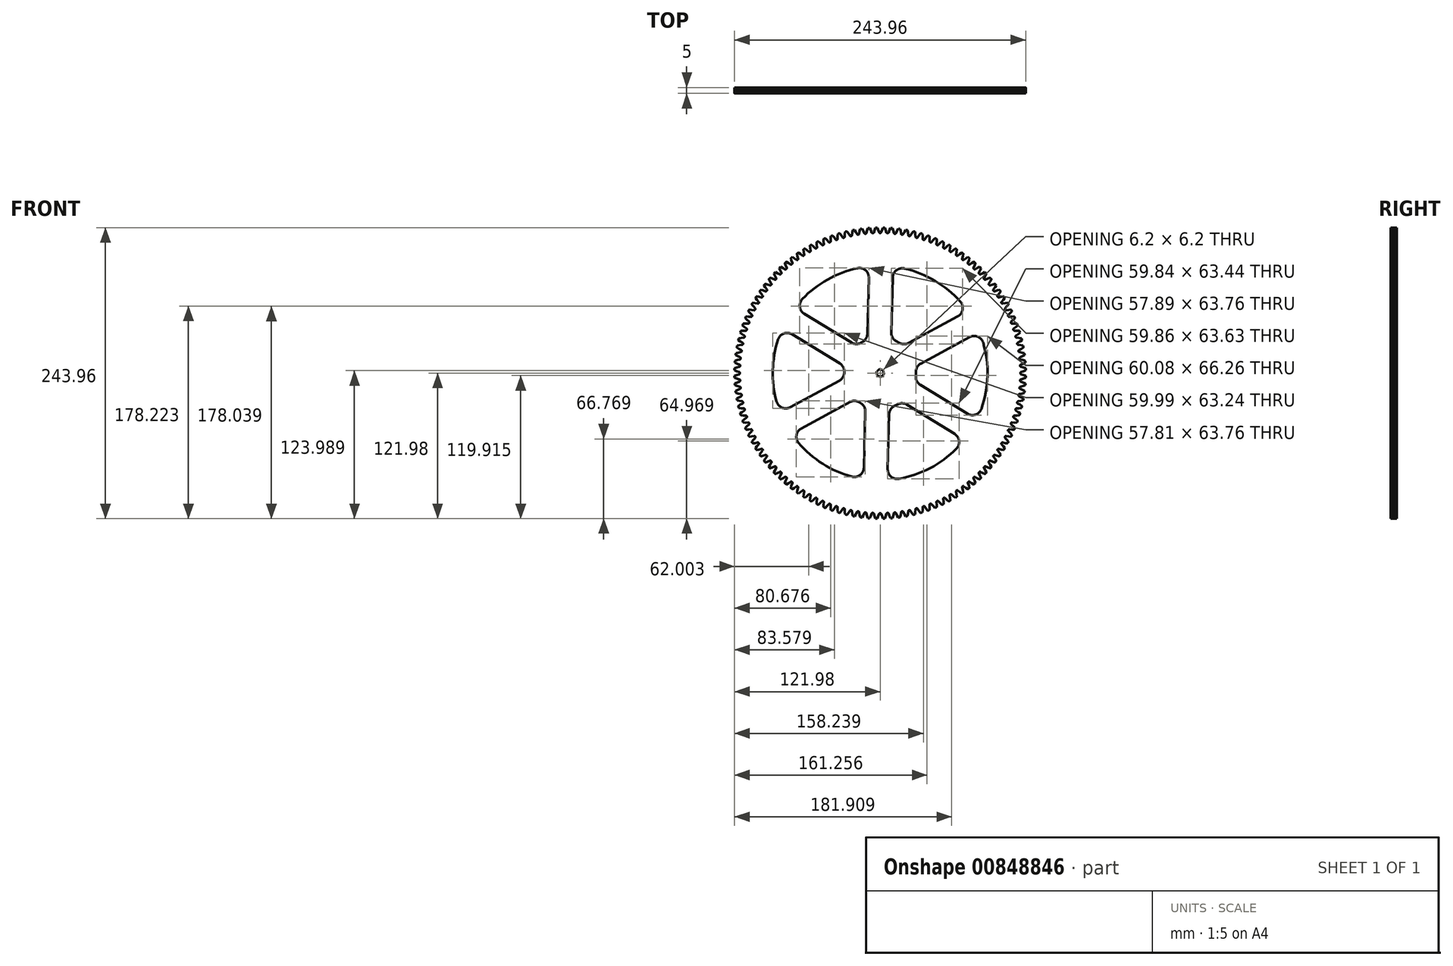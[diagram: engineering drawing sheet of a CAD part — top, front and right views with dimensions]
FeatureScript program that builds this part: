
annotation { "Feature Type Name" : "Feature", "Feature Type Description" : "" }
export const myFeature = defineFeature(function(context is Context, id is Id, definition is map)
    precondition{}
    {
        {
            var Q0;
            Q0=qCreatedBy(makeId("Front.planeOp"),FACE);
            var sketch = newSketch(context, id + "F0", { "sketchPlane" : qUnion([Q0])});
            skArc(sketch, "E0", {"start": v(-16.1, -25.31) * mm, "mid": v(-16.55, -25.02) * mm, "end": v(-16.99, -24.73) * mm});
            skArc(sketch, "E1", {"start": v(-16.1, -25.31) * mm, "mid": v(-13.33, -28.3) * mm, "end": v(-12.4, -32.27) * mm});
            skLineSegment(sketch, "E2", {"start": v(-12.4, -32.27) * mm, "end": v(-13.63, -79.3) * mm});
            skArc(sketch, "E3", {"start": v(-13.63, -79.3) * mm, "mid": v(-16.86, -85.52) * mm, "end": v(-23.74, -86.81) * mm});
            skArc(sketch, "E4", {"start": v(-23.74, -86.81) * mm, "mid": v(-48.12, -76.05) * mm, "end": v(-68.28, -58.63) * mm});
            skArc(sketch, "E5", {"start": v(-68.28, -58.63) * mm, "mid": v(-70.08, -51.97) * mm, "end": v(-66.03, -46.39) * mm});
            skLineSegment(sketch, "E6", {"start": v(-25.33, -24.3) * mm, "end": v(-66.03, -46.39) * mm});
            skArc(sketch, "E7", {"start": v(-25.33, -24.3) * mm, "mid": v(-21.1, -23.33) * mm, "end": v(-16.99, -24.73) * mm});
            skArc(sketch, "E8", {"start": v(-30, 0.55) * mm, "mid": v(-30, 0.75) * mm, "end": v(-29.98, 0.96) * mm});
            skArc(sketch, "E9", {"start": v(-30, 0.55) * mm, "mid": v(-31.16, -3.46) * mm, "end": v(-34.18, -6.33) * mm});
            skLineSegment(sketch, "E10", {"start": v(-34.18, -6.33) * mm, "end": v(-75.28, -28.65) * mm});
            skArc(sketch, "E11", {"start": v(-75.28, -28.65) * mm, "mid": v(-82.24, -28.98) * mm, "end": v(-86.82, -23.73) * mm});
            skArc(sketch, "E12", {"start": v(-86.82, -23.73) * mm, "mid": v(-89.97, 2.32) * mm, "end": v(-85.48, 28.17) * mm});
            skArc(sketch, "E13", {"start": v(-85.48, 28.17) * mm, "mid": v(-80.63, 33.18) * mm, "end": v(-73.7, 32.49) * mm});
            skLineSegment(sketch, "E14", {"start": v(-33.8, 8.04) * mm, "end": v(-73.7, 32.49) * mm});
            skArc(sketch, "E15", {"start": v(-33.8, 8.04) * mm, "mid": v(-30.94, 5.01) * mm, "end": v(-29.98, 0.96) * mm});
            skLineSegment(sketch, "E16", {"start": v(34.17, 8.01) * mm, "end": v(74.87, 30.1) * mm});
            skArc(sketch, "E17", {"start": v(74.87, 30.1) * mm, "mid": v(81.76, 30.46) * mm, "end": v(86.36, 25.33) * mm});
            skArc(sketch, "E18", {"start": v(86.36, 25.33) * mm, "mid": v(89.97, -2.4) * mm, "end": v(84.89, -29.9) * mm});
            skArc(sketch, "E19", {"start": v(84.89, -29.9) * mm, "mid": v(80.02, -34.78) * mm, "end": v(73.16, -34.06) * mm});
            skLineSegment(sketch, "E20", {"start": v(33.7, -9.87) * mm, "end": v(73.16, -34.06) * mm});
            skArc(sketch, "E21", {"start": v(33.7, -9.87) * mm, "mid": v(30.75, -6.68) * mm, "end": v(29.9, -2.4) * mm});
            skArc(sketch, "E22", {"start": v(29.99, 0.78) * mm, "mid": v(29.99, -0.82) * mm, "end": v(29.9, -2.4) * mm});
            skArc(sketch, "E23", {"start": v(29.99, 0.78) * mm, "mid": v(31.06, 4.98) * mm, "end": v(34.17, 8.01) * mm});
            skArc(sketch, "E24", {"start": v(13.7, 26.7) * mm, "mid": v(14.8, 26.1) * mm, "end": v(15.88, 25.45) * mm});
            skArc(sketch, "E25", {"start": v(13.7, 26.7) * mm, "mid": v(10.46, 29.73) * mm, "end": v(9.35, 34.02) * mm});
            skLineSegment(sketch, "E26", {"start": v(9.35, 34.02) * mm, "end": v(10.55, 80.08) * mm});
            skArc(sketch, "E27", {"start": v(10.55, 80.08) * mm, "mid": v(13.66, 86.2) * mm, "end": v(20.36, 87.67) * mm});
            skArc(sketch, "E28", {"start": v(20.36, 87.67) * mm, "mid": v(45.93, 77.4) * mm, "end": v(67.19, 59.88) * mm});
            skArc(sketch, "E29", {"start": v(67.19, 59.88) * mm, "mid": v(69.1, 53.18) * mm, "end": v(65.03, 47.53) * mm});
            skLineSegment(sketch, "E30", {"start": v(23.93, 25.21) * mm, "end": v(65.03, 47.53) * mm});
            skArc(sketch, "E31", {"start": v(23.93, 25.21) * mm, "mid": v(19.87, 24.25) * mm, "end": v(15.88, 25.45) * mm});
            skArc(sketch, "E32", {"start": v(12.05, 116.88) * mm, "mid": v(12.28, 116.86) * mm, "end": v(12.52, 116.83) * mm});
            skArc(sketch, "E33", {"start": v(12.05, 116.88) * mm, "mid": v(11.67, 117.05) * mm, "end": v(11.47, 117.4) * mm});
            skLineSegment(sketch, "E34", {"start": v(10.94, 119.67) * mm, "end": v(10.38, 121.56) * mm});
            skLineSegment(sketch, "E35", {"start": v(11.47, 117.4) * mm, "end": v(10.94, 119.67) * mm});
            skArc(sketch, "E36", {"start": v(8.76, 121.68) * mm, "mid": v(9.57, 121.62) * mm, "end": v(10.38, 121.56) * mm});
            skLineSegment(sketch, "E37", {"start": v(7.92, 119.9) * mm, "end": v(8.76, 121.68) * mm});
            skLineSegment(sketch, "E38", {"start": v(7.04, 117.75) * mm, "end": v(7.92, 119.9) * mm});
            skArc(sketch, "E39", {"start": v(7.04, 117.75) * mm, "mid": v(6.78, 117.43) * mm, "end": v(6.39, 117.33) * mm});
            skArc(sketch, "E40", {"start": v(5.91, 117.35) * mm, "mid": v(6.15, 117.34) * mm, "end": v(6.39, 117.33) * mm});
            skArc(sketch, "E41", {"start": v(5.91, 117.35) * mm, "mid": v(5.53, 117.5) * mm, "end": v(5.3, 117.84) * mm});
            skLineSegment(sketch, "E42", {"start": v(4.66, 120.08) * mm, "end": v(4, 121.93) * mm});
            skLineSegment(sketch, "E43", {"start": v(5.3, 117.84) * mm, "end": v(4.66, 120.08) * mm});
            skArc(sketch, "E44", {"start": v(2.38, 121.98) * mm, "mid": v(3.2, 121.96) * mm, "end": v(4, 121.93) * mm});
            skLineSegment(sketch, "E45", {"start": v(1.63, 120.15) * mm, "end": v(2.38, 121.98) * mm});
            skLineSegment(sketch, "E46", {"start": v(0.86, 117.96) * mm, "end": v(1.63, 120.15) * mm});
            skArc(sketch, "E47", {"start": v(0.86, 117.96) * mm, "mid": v(0.63, 117.63) * mm, "end": v(0.24, 117.5) * mm});
            skArc(sketch, "E48", {"start": v(-0.24, 117.5) * mm, "mid": v(0, 117.5) * mm, "end": v(0.24, 117.5) * mm});
            skArc(sketch, "E49", {"start": v(-0.24, 117.5) * mm, "mid": v(-0.63, 117.63) * mm, "end": v(-0.86, 117.96) * mm});
            skLineSegment(sketch, "E50", {"start": v(-1.63, 120.15) * mm, "end": v(-2.38, 121.98) * mm});
            skLineSegment(sketch, "E51", {"start": v(-0.86, 117.96) * mm, "end": v(-1.63, 120.15) * mm});
            skArc(sketch, "E52", {"start": v(-4, 121.93) * mm, "mid": v(-3.2, 121.96) * mm, "end": v(-2.38, 121.98) * mm});
            skLineSegment(sketch, "E53", {"start": v(-4.66, 120.08) * mm, "end": v(-4, 121.93) * mm});
            skLineSegment(sketch, "E54", {"start": v(-5.3, 117.84) * mm, "end": v(-4.66, 120.08) * mm});
            skArc(sketch, "E55", {"start": v(-5.3, 117.84) * mm, "mid": v(-5.53, 117.5) * mm, "end": v(-5.91, 117.35) * mm});
            skArc(sketch, "E56", {"start": v(-6.39, 117.33) * mm, "mid": v(-6.15, 117.34) * mm, "end": v(-5.91, 117.35) * mm});
            skArc(sketch, "E57", {"start": v(-6.39, 117.33) * mm, "mid": v(-6.78, 117.43) * mm, "end": v(-7.04, 117.75) * mm});
            skLineSegment(sketch, "E58", {"start": v(-7.92, 119.9) * mm, "end": v(-8.76, 121.68) * mm});
            skLineSegment(sketch, "E59", {"start": v(-7.04, 117.75) * mm, "end": v(-7.92, 119.9) * mm});
            skArc(sketch, "E60", {"start": v(-10.38, 121.56) * mm, "mid": v(-9.57, 121.62) * mm, "end": v(-8.76, 121.68) * mm});
            skLineSegment(sketch, "E61", {"start": v(-10.94, 119.67) * mm, "end": v(-10.38, 121.56) * mm});
            skLineSegment(sketch, "E62", {"start": v(-11.47, 117.4) * mm, "end": v(-10.94, 119.67) * mm});
            skArc(sketch, "E63", {"start": v(-11.47, 117.4) * mm, "mid": v(-11.67, 117.05) * mm, "end": v(-12.05, 116.88) * mm});
            skArc(sketch, "E64", {"start": v(-12.52, 116.83) * mm, "mid": v(-12.28, 116.86) * mm, "end": v(-12.05, 116.88) * mm});
            skArc(sketch, "E65", {"start": v(-12.52, 116.83) * mm, "mid": v(-12.92, 116.92) * mm, "end": v(-13.19, 117.22) * mm});
            skLineSegment(sketch, "E66", {"start": v(-14.18, 119.33) * mm, "end": v(-15.12, 121.06) * mm});
            skLineSegment(sketch, "E67", {"start": v(-13.19, 117.22) * mm, "end": v(-14.18, 119.33) * mm});
            skArc(sketch, "E68", {"start": v(-16.73, 120.85) * mm, "mid": v(-15.92, 120.96) * mm, "end": v(-15.12, 121.06) * mm});
            skLineSegment(sketch, "E69", {"start": v(-17.18, 118.93) * mm, "end": v(-16.73, 120.85) * mm});
            skLineSegment(sketch, "E70", {"start": v(-17.6, 116.64) * mm, "end": v(-17.18, 118.93) * mm});
            skArc(sketch, "E71", {"start": v(-17.6, 116.64) * mm, "mid": v(-17.78, 116.28) * mm, "end": v(-18.15, 116.1) * mm});
            skArc(sketch, "E72", {"start": v(-18.62, 116.02) * mm, "mid": v(-18.38, 116.05) * mm, "end": v(-18.15, 116.1) * mm});
            skArc(sketch, "E73", {"start": v(-18.62, 116.02) * mm, "mid": v(-19.02, 116.08) * mm, "end": v(-19.3, 116.37) * mm});
            skLineSegment(sketch, "E74", {"start": v(-20.4, 118.42) * mm, "end": v(-21.44, 120.1) * mm});
            skLineSegment(sketch, "E75", {"start": v(-19.3, 116.37) * mm, "end": v(-20.4, 118.42) * mm});
            skArc(sketch, "E76", {"start": v(-23.03, 119.8) * mm, "mid": v(-22.23, 119.96) * mm, "end": v(-21.44, 120.1) * mm});
            skLineSegment(sketch, "E77", {"start": v(-23.38, 117.87) * mm, "end": v(-23.03, 119.8) * mm});
            skLineSegment(sketch, "E78", {"start": v(-23.68, 115.56) * mm, "end": v(-23.38, 117.87) * mm});
            skArc(sketch, "E79", {"start": v(-23.68, 115.56) * mm, "mid": v(-23.84, 115.19) * mm, "end": v(-24.2, 114.98) * mm});
            skArc(sketch, "E80", {"start": v(-24.66, 114.88) * mm, "mid": v(-24.43, 114.93) * mm, "end": v(-24.2, 114.98) * mm});
            skArc(sketch, "E81", {"start": v(-24.66, 114.88) * mm, "mid": v(-25.07, 114.93) * mm, "end": v(-25.37, 115.2) * mm});
            skLineSegment(sketch, "E82", {"start": v(-26.58, 117.19) * mm, "end": v(-27.7, 118.82) * mm});
            skLineSegment(sketch, "E83", {"start": v(-25.37, 115.2) * mm, "end": v(-26.58, 117.19) * mm});
            skArc(sketch, "E84", {"start": v(-29.27, 118.44) * mm, "mid": v(-28.48, 118.63) * mm, "end": v(-27.7, 118.82) * mm});
            skLineSegment(sketch, "E85", {"start": v(-29.52, 116.48) * mm, "end": v(-29.27, 118.44) * mm});
            skLineSegment(sketch, "E86", {"start": v(-29.7, 114.16) * mm, "end": v(-29.52, 116.48) * mm});
            skArc(sketch, "E87", {"start": v(-29.7, 114.16) * mm, "mid": v(-29.84, 113.78) * mm, "end": v(-30.18, 113.56) * mm});
            skArc(sketch, "E88", {"start": v(-30.64, 113.43) * mm, "mid": v(-30.41, 113.5) * mm, "end": v(-30.18, 113.56) * mm});
            skArc(sketch, "E89", {"start": v(-30.64, 113.43) * mm, "mid": v(-31.05, 113.46) * mm, "end": v(-31.36, 113.71) * mm});
            skLineSegment(sketch, "E90", {"start": v(-32.68, 115.64) * mm, "end": v(-33.87, 117.2) * mm});
            skLineSegment(sketch, "E91", {"start": v(-31.36, 113.71) * mm, "end": v(-32.68, 115.64) * mm});
            skArc(sketch, "E92", {"start": v(-35.43, 116.74) * mm, "mid": v(-34.65, 116.98) * mm, "end": v(-33.87, 117.2) * mm});
            skLineSegment(sketch, "E93", {"start": v(-35.58, 114.78) * mm, "end": v(-35.43, 116.74) * mm});
            skLineSegment(sketch, "E94", {"start": v(-35.63, 112.45) * mm, "end": v(-35.58, 114.78) * mm});
            skArc(sketch, "E95", {"start": v(-35.63, 112.45) * mm, "mid": v(-35.75, 112.06) * mm, "end": v(-36.08, 111.82) * mm});
            skArc(sketch, "E96", {"start": v(-36.54, 111.68) * mm, "mid": v(-36.3, 111.75) * mm, "end": v(-36.08, 111.82) * mm});
            skArc(sketch, "E97", {"start": v(-36.54, 111.68) * mm, "mid": v(-36.94, 111.68) * mm, "end": v(-37.27, 111.92) * mm});
            skLineSegment(sketch, "E98", {"start": v(-38.68, 113.77) * mm, "end": v(-39.96, 115.27) * mm});
            skLineSegment(sketch, "E99", {"start": v(-37.27, 111.92) * mm, "end": v(-38.68, 113.77) * mm});
            skArc(sketch, "E100", {"start": v(-41.49, 114.73) * mm, "mid": v(-40.72, 115) * mm, "end": v(-39.96, 115.27) * mm});
            skLineSegment(sketch, "E101", {"start": v(-41.54, 112.76) * mm, "end": v(-41.49, 114.73) * mm});
            skLineSegment(sketch, "E102", {"start": v(-41.47, 110.43) * mm, "end": v(-41.54, 112.76) * mm});
            skArc(sketch, "E103", {"start": v(-41.47, 110.43) * mm, "mid": v(-41.57, 110.04) * mm, "end": v(-41.89, 109.78) * mm});
            skArc(sketch, "E104", {"start": v(-42.33, 109.61) * mm, "mid": v(-42.1, 109.7) * mm, "end": v(-41.89, 109.78) * mm});
            skArc(sketch, "E105", {"start": v(-42.33, 109.61) * mm, "mid": v(-42.74, 109.59) * mm, "end": v(-43.08, 109.81) * mm});
            skLineSegment(sketch, "E106", {"start": v(-44.58, 111.59) * mm, "end": v(-45.94, 113.02) * mm});
            skLineSegment(sketch, "E107", {"start": v(-43.08, 109.81) * mm, "end": v(-44.58, 111.59) * mm});
            skArc(sketch, "E108", {"start": v(-47.43, 112.4) * mm, "mid": v(-46.69, 112.71) * mm, "end": v(-45.94, 113.02) * mm});
            skLineSegment(sketch, "E109", {"start": v(-47.38, 110.43) * mm, "end": v(-47.43, 112.4) * mm});
            skLineSegment(sketch, "E110", {"start": v(-47.19, 108.11) * mm, "end": v(-47.38, 110.43) * mm});
            skArc(sketch, "E111", {"start": v(-47.19, 108.11) * mm, "mid": v(-47.27, 107.71) * mm, "end": v(-47.57, 107.44) * mm});
            skArc(sketch, "E112", {"start": v(-48, 107.24) * mm, "mid": v(-47.8, 107.34) * mm, "end": v(-47.57, 107.44) * mm});
            skArc(sketch, "E113", {"start": v(-48, 107.24) * mm, "mid": v(-48.42, 107.2) * mm, "end": v(-48.77, 107.4) * mm});
            skLineSegment(sketch, "E114", {"start": v(-50.36, 109.1) * mm, "end": v(-51.8, 110.46) * mm});
            skLineSegment(sketch, "E115", {"start": v(-48.77, 107.4) * mm, "end": v(-50.36, 109.1) * mm});
            skArc(sketch, "E116", {"start": v(-53.25, 109.76) * mm, "mid": v(-52.52, 110.12) * mm, "end": v(-51.8, 110.46) * mm});
            skLineSegment(sketch, "E117", {"start": v(-53.1, 107.8) * mm, "end": v(-53.25, 109.76) * mm});
            skLineSegment(sketch, "E118", {"start": v(-52.78, 105.5) * mm, "end": v(-53.1, 107.8) * mm});
            skArc(sketch, "E119", {"start": v(-52.78, 105.5) * mm, "mid": v(-52.84, 105.1) * mm, "end": v(-53.13, 104.8) * mm});
            skArc(sketch, "E120", {"start": v(-53.56, 104.58) * mm, "mid": v(-53.34, 104.7) * mm, "end": v(-53.13, 104.8) * mm});
            skArc(sketch, "E121", {"start": v(-53.56, 104.58) * mm, "mid": v(-53.96, 104.52) * mm, "end": v(-54.32, 104.7) * mm});
            skLineSegment(sketch, "E122", {"start": v(-56, 106.32) * mm, "end": v(-57.5, 107.6) * mm});
            skLineSegment(sketch, "E123", {"start": v(-54.32, 104.7) * mm, "end": v(-56, 106.32) * mm});
            skArc(sketch, "E124", {"start": v(-58.92, 106.83) * mm, "mid": v(-58.21, 107.22) * mm, "end": v(-57.5, 107.6) * mm});
            skLineSegment(sketch, "E125", {"start": v(-58.66, 104.87) * mm, "end": v(-58.92, 106.83) * mm});
            skLineSegment(sketch, "E126", {"start": v(-58.23, 102.59) * mm, "end": v(-58.66, 104.87) * mm});
            skArc(sketch, "E127", {"start": v(-58.23, 102.59) * mm, "mid": v(-58.27, 102.18) * mm, "end": v(-58.54, 101.88) * mm});
            skArc(sketch, "E128", {"start": v(-58.96, 101.64) * mm, "mid": v(-58.75, 101.76) * mm, "end": v(-58.54, 101.88) * mm});
            skArc(sketch, "E129", {"start": v(-58.96, 101.64) * mm, "mid": v(-59.36, 101.55) * mm, "end": v(-59.73, 101.72) * mm});
            skLineSegment(sketch, "E130", {"start": v(-61.5, 103.24) * mm, "end": v(-63.05, 104.44) * mm});
            skLineSegment(sketch, "E131", {"start": v(-59.73, 101.72) * mm, "end": v(-61.5, 103.24) * mm});
            skArc(sketch, "E132", {"start": v(-64.43, 103.6) * mm, "mid": v(-63.74, 104.02) * mm, "end": v(-63.05, 104.44) * mm});
            skLineSegment(sketch, "E133", {"start": v(-64.07, 101.66) * mm, "end": v(-64.43, 103.6) * mm});
            skLineSegment(sketch, "E134", {"start": v(-63.52, 99.4) * mm, "end": v(-64.07, 101.66) * mm});
            skArc(sketch, "E135", {"start": v(-63.52, 99.4) * mm, "mid": v(-63.54, 99) * mm, "end": v(-63.8, 98.67) * mm});
            skArc(sketch, "E136", {"start": v(-64.2, 98.41) * mm, "mid": v(-64, 98.54) * mm, "end": v(-63.8, 98.67) * mm});
            skArc(sketch, "E137", {"start": v(-64.2, 98.41) * mm, "mid": v(-64.59, 98.3) * mm, "end": v(-64.97, 98.46) * mm});
            skLineSegment(sketch, "E138", {"start": v(-66.8, 99.88) * mm, "end": v(-68.43, 101) * mm});
            skLineSegment(sketch, "E139", {"start": v(-64.97, 98.46) * mm, "end": v(-66.8, 99.88) * mm});
            skArc(sketch, "E140", {"start": v(-69.77, 100.08) * mm, "mid": v(-69.1, 100.54) * mm, "end": v(-68.43, 101) * mm});
            skLineSegment(sketch, "E141", {"start": v(-69.3, 98.17) * mm, "end": v(-69.77, 100.08) * mm});
            skLineSegment(sketch, "E142", {"start": v(-68.63, 95.94) * mm, "end": v(-69.3, 98.17) * mm});
            skArc(sketch, "E143", {"start": v(-68.63, 95.94) * mm, "mid": v(-68.63, 95.53) * mm, "end": v(-68.87, 95.2) * mm});
            skArc(sketch, "E144", {"start": v(-69.26, 94.92) * mm, "mid": v(-69.06, 95.06) * mm, "end": v(-68.87, 95.2) * mm});
            skArc(sketch, "E145", {"start": v(-69.26, 94.92) * mm, "mid": v(-69.65, 94.8) * mm, "end": v(-70.03, 94.92) * mm});
            skLineSegment(sketch, "E146", {"start": v(-71.95, 96.25) * mm, "end": v(-73.62, 97.28) * mm});
            skLineSegment(sketch, "E147", {"start": v(-70.03, 94.92) * mm, "end": v(-71.95, 96.25) * mm});
            skArc(sketch, "E148", {"start": v(-74.9, 96.3) * mm, "mid": v(-74.27, 96.79) * mm, "end": v(-73.62, 97.28) * mm});
            skLineSegment(sketch, "E149", {"start": v(-74.35, 94.4) * mm, "end": v(-74.9, 96.3) * mm});
            skLineSegment(sketch, "E150", {"start": v(-73.56, 92.21) * mm, "end": v(-74.35, 94.4) * mm});
            skArc(sketch, "E151", {"start": v(-73.56, 92.21) * mm, "mid": v(-73.54, 91.8) * mm, "end": v(-73.76, 91.46) * mm});
            skArc(sketch, "E152", {"start": v(-74.13, 91.16) * mm, "mid": v(-73.95, 91.31) * mm, "end": v(-73.76, 91.46) * mm});
            skArc(sketch, "E153", {"start": v(-74.13, 91.16) * mm, "mid": v(-74.51, 91.02) * mm, "end": v(-74.9, 91.13) * mm});
            skLineSegment(sketch, "E154", {"start": v(-76.88, 92.35) * mm, "end": v(-78.62, 93.3) * mm});
            skLineSegment(sketch, "E155", {"start": v(-74.9, 91.13) * mm, "end": v(-76.88, 92.35) * mm});
            skArc(sketch, "E156", {"start": v(-79.85, 92.24) * mm, "mid": v(-79.23, 92.77) * mm, "end": v(-78.62, 93.3) * mm});
            skLineSegment(sketch, "E157", {"start": v(-79.19, 90.38) * mm, "end": v(-79.85, 92.24) * mm});
            skLineSegment(sketch, "E158", {"start": v(-78.29, 88.24) * mm, "end": v(-79.19, 90.38) * mm});
            skArc(sketch, "E159", {"start": v(-78.29, 88.24) * mm, "mid": v(-78.24, 87.83) * mm, "end": v(-78.45, 87.48) * mm});
            skArc(sketch, "E160", {"start": v(-78.8, 87.16) * mm, "mid": v(-78.62, 87.32) * mm, "end": v(-78.45, 87.48) * mm});
            skArc(sketch, "E161", {"start": v(-78.8, 87.16) * mm, "mid": v(-79.17, 87) * mm, "end": v(-79.57, 87.08) * mm});
            skLineSegment(sketch, "E162", {"start": v(-81.61, 88.2) * mm, "end": v(-83.4, 89.05) * mm});
            skLineSegment(sketch, "E163", {"start": v(-79.57, 87.08) * mm, "end": v(-81.61, 88.2) * mm});
            skArc(sketch, "E164", {"start": v(-84.56, 87.94) * mm, "mid": v(-83.98, 88.5) * mm, "end": v(-83.4, 89.05) * mm});
            skLineSegment(sketch, "E165", {"start": v(-83.8, 86.12) * mm, "end": v(-84.56, 87.94) * mm});
            skLineSegment(sketch, "E166", {"start": v(-82.8, 84.02) * mm, "end": v(-83.8, 86.12) * mm});
            skArc(sketch, "E167", {"start": v(-82.8, 84.02) * mm, "mid": v(-82.73, 83.62) * mm, "end": v(-82.92, 83.25) * mm});
            skArc(sketch, "E168", {"start": v(-83.25, 82.92) * mm, "mid": v(-83.09, 83.09) * mm, "end": v(-82.92, 83.25) * mm});
            skArc(sketch, "E169", {"start": v(-83.25, 82.92) * mm, "mid": v(-83.62, 82.73) * mm, "end": v(-84.02, 82.8) * mm});
            skLineSegment(sketch, "E170", {"start": v(-86.12, 83.8) * mm, "end": v(-87.94, 84.56) * mm});
            skLineSegment(sketch, "E171", {"start": v(-84.02, 82.8) * mm, "end": v(-86.12, 83.8) * mm});
            skArc(sketch, "E172", {"start": v(-89.05, 83.4) * mm, "mid": v(-88.5, 83.98) * mm, "end": v(-87.94, 84.56) * mm});
            skLineSegment(sketch, "E173", {"start": v(-88.2, 81.61) * mm, "end": v(-89.05, 83.4) * mm});
            skLineSegment(sketch, "E174", {"start": v(-87.08, 79.57) * mm, "end": v(-88.2, 81.61) * mm});
            skArc(sketch, "E175", {"start": v(-87.08, 79.57) * mm, "mid": v(-87, 79.17) * mm, "end": v(-87.16, 78.8) * mm});
            skArc(sketch, "E176", {"start": v(-87.48, 78.45) * mm, "mid": v(-87.32, 78.62) * mm, "end": v(-87.16, 78.8) * mm});
            skArc(sketch, "E177", {"start": v(-87.48, 78.45) * mm, "mid": v(-87.83, 78.24) * mm, "end": v(-88.24, 78.29) * mm});
            skLineSegment(sketch, "E178", {"start": v(-90.38, 79.19) * mm, "end": v(-92.24, 79.85) * mm});
            skLineSegment(sketch, "E179", {"start": v(-88.24, 78.29) * mm, "end": v(-90.38, 79.19) * mm});
            skArc(sketch, "E180", {"start": v(-93.3, 78.62) * mm, "mid": v(-92.77, 79.23) * mm, "end": v(-92.24, 79.85) * mm});
            skLineSegment(sketch, "E181", {"start": v(-92.35, 76.88) * mm, "end": v(-93.3, 78.62) * mm});
            skLineSegment(sketch, "E182", {"start": v(-91.13, 74.9) * mm, "end": v(-92.35, 76.88) * mm});
            skArc(sketch, "E183", {"start": v(-91.13, 74.9) * mm, "mid": v(-91.02, 74.51) * mm, "end": v(-91.16, 74.13) * mm});
            skArc(sketch, "E184", {"start": v(-91.46, 73.76) * mm, "mid": v(-91.31, 73.95) * mm, "end": v(-91.16, 74.13) * mm});
            skArc(sketch, "E185", {"start": v(-91.46, 73.76) * mm, "mid": v(-91.8, 73.54) * mm, "end": v(-92.21, 73.56) * mm});
            skLineSegment(sketch, "E186", {"start": v(-94.4, 74.35) * mm, "end": v(-96.3, 74.9) * mm});
            skLineSegment(sketch, "E187", {"start": v(-92.21, 73.56) * mm, "end": v(-94.4, 74.35) * mm});
            skArc(sketch, "E188", {"start": v(-97.28, 73.62) * mm, "mid": v(-96.79, 74.27) * mm, "end": v(-96.3, 74.9) * mm});
            skLineSegment(sketch, "E189", {"start": v(-96.25, 71.95) * mm, "end": v(-97.28, 73.62) * mm});
            skLineSegment(sketch, "E190", {"start": v(-94.92, 70.03) * mm, "end": v(-96.25, 71.95) * mm});
            skArc(sketch, "E191", {"start": v(-94.92, 70.03) * mm, "mid": v(-94.8, 69.65) * mm, "end": v(-94.92, 69.26) * mm});
            skArc(sketch, "E192", {"start": v(-95.2, 68.87) * mm, "mid": v(-95.06, 69.06) * mm, "end": v(-94.92, 69.26) * mm});
            skArc(sketch, "E193", {"start": v(-95.2, 68.87) * mm, "mid": v(-95.53, 68.63) * mm, "end": v(-95.94, 68.63) * mm});
            skLineSegment(sketch, "E194", {"start": v(-98.17, 69.3) * mm, "end": v(-100.08, 69.77) * mm});
            skLineSegment(sketch, "E195", {"start": v(-95.94, 68.63) * mm, "end": v(-98.17, 69.3) * mm});
            skArc(sketch, "E196", {"start": v(-101, 68.43) * mm, "mid": v(-100.54, 69.1) * mm, "end": v(-100.08, 69.77) * mm});
            skLineSegment(sketch, "E197", {"start": v(-99.88, 66.8) * mm, "end": v(-101, 68.43) * mm});
            skLineSegment(sketch, "E198", {"start": v(-98.46, 64.97) * mm, "end": v(-99.88, 66.8) * mm});
            skArc(sketch, "E199", {"start": v(-98.46, 64.97) * mm, "mid": v(-98.3, 64.59) * mm, "end": v(-98.41, 64.2) * mm});
            skArc(sketch, "E200", {"start": v(-98.67, 63.8) * mm, "mid": v(-98.54, 64) * mm, "end": v(-98.41, 64.2) * mm});
            skArc(sketch, "E201", {"start": v(-98.67, 63.8) * mm, "mid": v(-99, 63.54) * mm, "end": v(-99.4, 63.52) * mm});
            skLineSegment(sketch, "E202", {"start": v(-101.66, 64.07) * mm, "end": v(-103.6, 64.43) * mm});
            skLineSegment(sketch, "E203", {"start": v(-99.4, 63.52) * mm, "end": v(-101.66, 64.07) * mm});
            skArc(sketch, "E204", {"start": v(-104.44, 63.05) * mm, "mid": v(-104.02, 63.74) * mm, "end": v(-103.6, 64.43) * mm});
            skLineSegment(sketch, "E205", {"start": v(-103.24, 61.5) * mm, "end": v(-104.44, 63.05) * mm});
            skLineSegment(sketch, "E206", {"start": v(-101.72, 59.73) * mm, "end": v(-103.24, 61.5) * mm});
            skArc(sketch, "E207", {"start": v(-101.72, 59.73) * mm, "mid": v(-101.55, 59.36) * mm, "end": v(-101.64, 58.96) * mm});
            skArc(sketch, "E208", {"start": v(-101.88, 58.54) * mm, "mid": v(-101.76, 58.75) * mm, "end": v(-101.64, 58.96) * mm});
            skArc(sketch, "E209", {"start": v(-101.88, 58.54) * mm, "mid": v(-102.18, 58.27) * mm, "end": v(-102.59, 58.23) * mm});
            skArc(sketch, "E210", {"start": v(1.55, -2.68) * mm, "mid": v(0.8, -3) * mm, "end": v(0, -3.1) * mm});
            skLineSegment(sketch, "E211", {"start": v(1.45, -2.51) * mm, "end": v(1.55, -2.68) * mm});
            skArc(sketch, "E212", {"start": v(2.51, -1.45) * mm, "mid": v(2.05, -2.05) * mm, "end": v(1.45, -2.51) * mm});
            skLineSegment(sketch, "E213", {"start": v(2.51, -1.45) * mm, "end": v(2.68, -1.55) * mm});
            skArc(sketch, "E214", {"start": v(3.1, 0) * mm, "mid": v(3, -0.8) * mm, "end": v(2.68, -1.55) * mm});
            skLineSegment(sketch, "E215", {"start": v(2.9, 0) * mm, "end": v(3.1, 0) * mm});
            skArc(sketch, "E216", {"start": v(2.51, 1.45) * mm, "mid": v(2.8, 0.75) * mm, "end": v(2.9, 0) * mm});
            skLineSegment(sketch, "E217", {"start": v(2.51, 1.45) * mm, "end": v(2.68, 1.55) * mm});
            skArc(sketch, "E218", {"start": v(1.55, 2.68) * mm, "mid": v(2.2, 2.2) * mm, "end": v(2.68, 1.55) * mm});
            skLineSegment(sketch, "E219", {"start": v(1.45, 2.51) * mm, "end": v(1.55, 2.68) * mm});
            skArc(sketch, "E220", {"start": v(0, 2.9) * mm, "mid": v(0.75, 2.8) * mm, "end": v(1.45, 2.51) * mm});
            skLineSegment(sketch, "E221", {"start": v(0, 2.9) * mm, "end": v(0, 3.1) * mm});
            skArc(sketch, "E222", {"start": v(-1.55, 2.68) * mm, "mid": v(-0.8, 3) * mm, "end": v(0, 3.1) * mm});
            skLineSegment(sketch, "E223", {"start": v(-1.45, 2.51) * mm, "end": v(-1.55, 2.68) * mm});
            skArc(sketch, "E224", {"start": v(-2.51, 1.45) * mm, "mid": v(-2.05, 2.05) * mm, "end": v(-1.45, 2.51) * mm});
            skLineSegment(sketch, "E225", {"start": v(-2.51, 1.45) * mm, "end": v(-2.68, 1.55) * mm});
            skArc(sketch, "E226", {"start": v(-3.1, 0) * mm, "mid": v(-3, 0.8) * mm, "end": v(-2.68, 1.55) * mm});
            skLineSegment(sketch, "E227", {"start": v(-2.9, 0) * mm, "end": v(-3.1, 0) * mm});
            skArc(sketch, "E228", {"start": v(-2.51, -1.45) * mm, "mid": v(-2.8, -0.75) * mm, "end": v(-2.9, 0) * mm});
            skLineSegment(sketch, "E229", {"start": v(-2.51, -1.45) * mm, "end": v(-2.68, -1.55) * mm});
            skArc(sketch, "E230", {"start": v(-1.55, -2.68) * mm, "mid": v(-2.2, -2.2) * mm, "end": v(-2.68, -1.55) * mm});
            skArc(sketch, "E231", {"start": v(13.19, 117.22) * mm, "mid": v(12.92, 116.92) * mm, "end": v(12.52, 116.83) * mm});
            skLineSegment(sketch, "E232", {"start": v(13.19, 117.22) * mm, "end": v(14.18, 119.33) * mm});
            skLineSegment(sketch, "E233", {"start": v(14.18, 119.33) * mm, "end": v(15.12, 121.06) * mm});
            skArc(sketch, "E234", {"start": v(15.12, 121.06) * mm, "mid": v(15.92, 120.96) * mm, "end": v(16.73, 120.85) * mm});
            skLineSegment(sketch, "E235", {"start": v(17.6, 116.64) * mm, "end": v(17.18, 118.93) * mm});
            skLineSegment(sketch, "E236", {"start": v(17.18, 118.93) * mm, "end": v(16.73, 120.85) * mm});
            skArc(sketch, "E237", {"start": v(18.15, 116.1) * mm, "mid": v(17.78, 116.28) * mm, "end": v(17.6, 116.64) * mm});
            skArc(sketch, "E238", {"start": v(18.15, 116.1) * mm, "mid": v(18.38, 116.05) * mm, "end": v(18.62, 116.02) * mm});
            skArc(sketch, "E239", {"start": v(19.3, 116.37) * mm, "mid": v(19.02, 116.08) * mm, "end": v(18.62, 116.02) * mm});
            skLineSegment(sketch, "E240", {"start": v(19.3, 116.37) * mm, "end": v(20.4, 118.42) * mm});
            skLineSegment(sketch, "E241", {"start": v(20.4, 118.42) * mm, "end": v(21.44, 120.1) * mm});
            skArc(sketch, "E242", {"start": v(21.44, 120.1) * mm, "mid": v(22.23, 119.96) * mm, "end": v(23.03, 119.8) * mm});
            skLineSegment(sketch, "E243", {"start": v(23.68, 115.56) * mm, "end": v(23.38, 117.87) * mm});
            skLineSegment(sketch, "E244", {"start": v(23.38, 117.87) * mm, "end": v(23.03, 119.8) * mm});
            skArc(sketch, "E245", {"start": v(24.2, 114.98) * mm, "mid": v(23.84, 115.19) * mm, "end": v(23.68, 115.56) * mm});
            skArc(sketch, "E246", {"start": v(24.2, 114.98) * mm, "mid": v(24.43, 114.93) * mm, "end": v(24.66, 114.88) * mm});
            skArc(sketch, "E247", {"start": v(25.37, 115.2) * mm, "mid": v(25.07, 114.93) * mm, "end": v(24.66, 114.88) * mm});
            skLineSegment(sketch, "E248", {"start": v(25.37, 115.2) * mm, "end": v(26.58, 117.19) * mm});
            skLineSegment(sketch, "E249", {"start": v(26.58, 117.19) * mm, "end": v(27.7, 118.82) * mm});
            skArc(sketch, "E250", {"start": v(27.7, 118.82) * mm, "mid": v(28.48, 118.63) * mm, "end": v(29.27, 118.44) * mm});
            skLineSegment(sketch, "E251", {"start": v(29.7, 114.16) * mm, "end": v(29.52, 116.48) * mm});
            skLineSegment(sketch, "E252", {"start": v(29.52, 116.48) * mm, "end": v(29.27, 118.44) * mm});
            skArc(sketch, "E253", {"start": v(30.18, 113.56) * mm, "mid": v(29.84, 113.78) * mm, "end": v(29.7, 114.16) * mm});
            skArc(sketch, "E254", {"start": v(30.18, 113.56) * mm, "mid": v(30.41, 113.5) * mm, "end": v(30.64, 113.43) * mm});
            skArc(sketch, "E255", {"start": v(31.36, 113.71) * mm, "mid": v(31.05, 113.46) * mm, "end": v(30.64, 113.43) * mm});
            skLineSegment(sketch, "E256", {"start": v(31.36, 113.71) * mm, "end": v(32.68, 115.64) * mm});
            skLineSegment(sketch, "E257", {"start": v(32.68, 115.64) * mm, "end": v(33.87, 117.2) * mm});
            skArc(sketch, "E258", {"start": v(33.87, 117.2) * mm, "mid": v(34.65, 116.98) * mm, "end": v(35.43, 116.74) * mm});
            skLineSegment(sketch, "E259", {"start": v(35.63, 112.45) * mm, "end": v(35.58, 114.78) * mm});
            skLineSegment(sketch, "E260", {"start": v(35.58, 114.78) * mm, "end": v(35.43, 116.74) * mm});
            skArc(sketch, "E261", {"start": v(36.08, 111.82) * mm, "mid": v(35.75, 112.06) * mm, "end": v(35.63, 112.45) * mm});
            skArc(sketch, "E262", {"start": v(36.08, 111.82) * mm, "mid": v(36.3, 111.75) * mm, "end": v(36.54, 111.68) * mm});
            skArc(sketch, "E263", {"start": v(37.27, 111.92) * mm, "mid": v(36.94, 111.68) * mm, "end": v(36.54, 111.68) * mm});
            skLineSegment(sketch, "E264", {"start": v(37.27, 111.92) * mm, "end": v(38.68, 113.77) * mm});
            skLineSegment(sketch, "E265", {"start": v(38.68, 113.77) * mm, "end": v(39.96, 115.27) * mm});
            skArc(sketch, "E266", {"start": v(39.96, 115.27) * mm, "mid": v(40.72, 115) * mm, "end": v(41.49, 114.73) * mm});
            skLineSegment(sketch, "E267", {"start": v(41.47, 110.43) * mm, "end": v(41.54, 112.76) * mm});
            skLineSegment(sketch, "E268", {"start": v(41.54, 112.76) * mm, "end": v(41.49, 114.73) * mm});
            skArc(sketch, "E269", {"start": v(41.89, 109.78) * mm, "mid": v(41.57, 110.04) * mm, "end": v(41.47, 110.43) * mm});
            skArc(sketch, "E270", {"start": v(41.89, 109.78) * mm, "mid": v(42.1, 109.7) * mm, "end": v(42.33, 109.61) * mm});
            skArc(sketch, "E271", {"start": v(43.08, 109.81) * mm, "mid": v(42.74, 109.59) * mm, "end": v(42.33, 109.61) * mm});
            skLineSegment(sketch, "E272", {"start": v(43.08, 109.81) * mm, "end": v(44.58, 111.59) * mm});
            skLineSegment(sketch, "E273", {"start": v(44.58, 111.59) * mm, "end": v(45.94, 113.02) * mm});
            skArc(sketch, "E274", {"start": v(45.94, 113.02) * mm, "mid": v(46.69, 112.71) * mm, "end": v(47.43, 112.4) * mm});
            skLineSegment(sketch, "E275", {"start": v(47.19, 108.11) * mm, "end": v(47.38, 110.43) * mm});
            skLineSegment(sketch, "E276", {"start": v(47.38, 110.43) * mm, "end": v(47.43, 112.4) * mm});
            skArc(sketch, "E277", {"start": v(47.57, 107.44) * mm, "mid": v(47.27, 107.71) * mm, "end": v(47.19, 108.11) * mm});
            skArc(sketch, "E278", {"start": v(47.57, 107.44) * mm, "mid": v(47.8, 107.34) * mm, "end": v(48, 107.24) * mm});
            skArc(sketch, "E279", {"start": v(48.77, 107.4) * mm, "mid": v(48.42, 107.2) * mm, "end": v(48, 107.24) * mm});
            skLineSegment(sketch, "E280", {"start": v(48.77, 107.4) * mm, "end": v(50.36, 109.1) * mm});
            skLineSegment(sketch, "E281", {"start": v(50.36, 109.1) * mm, "end": v(51.8, 110.46) * mm});
            skArc(sketch, "E282", {"start": v(51.8, 110.46) * mm, "mid": v(52.52, 110.12) * mm, "end": v(53.25, 109.76) * mm});
            skLineSegment(sketch, "E283", {"start": v(52.78, 105.5) * mm, "end": v(53.1, 107.8) * mm});
            skLineSegment(sketch, "E284", {"start": v(53.1, 107.8) * mm, "end": v(53.25, 109.76) * mm});
            skArc(sketch, "E285", {"start": v(53.13, 104.8) * mm, "mid": v(52.84, 105.1) * mm, "end": v(52.78, 105.5) * mm});
            skArc(sketch, "E286", {"start": v(53.13, 104.8) * mm, "mid": v(53.34, 104.7) * mm, "end": v(53.56, 104.58) * mm});
            skArc(sketch, "E287", {"start": v(54.32, 104.7) * mm, "mid": v(53.96, 104.52) * mm, "end": v(53.56, 104.58) * mm});
            skLineSegment(sketch, "E288", {"start": v(54.32, 104.7) * mm, "end": v(56, 106.32) * mm});
            skLineSegment(sketch, "E289", {"start": v(56, 106.32) * mm, "end": v(57.5, 107.6) * mm});
            skArc(sketch, "E290", {"start": v(57.5, 107.6) * mm, "mid": v(58.21, 107.22) * mm, "end": v(58.92, 106.83) * mm});
            skLineSegment(sketch, "E291", {"start": v(58.23, 102.59) * mm, "end": v(58.66, 104.87) * mm});
            skLineSegment(sketch, "E292", {"start": v(58.66, 104.87) * mm, "end": v(58.92, 106.83) * mm});
            skArc(sketch, "E293", {"start": v(58.54, 101.88) * mm, "mid": v(58.27, 102.18) * mm, "end": v(58.23, 102.59) * mm});
            skArc(sketch, "E294", {"start": v(58.54, 101.88) * mm, "mid": v(58.75, 101.76) * mm, "end": v(58.96, 101.64) * mm});
            skArc(sketch, "E295", {"start": v(59.73, 101.72) * mm, "mid": v(59.36, 101.55) * mm, "end": v(58.96, 101.64) * mm});
            skLineSegment(sketch, "E296", {"start": v(59.73, 101.72) * mm, "end": v(61.5, 103.24) * mm});
            skLineSegment(sketch, "E297", {"start": v(61.5, 103.24) * mm, "end": v(63.05, 104.44) * mm});
            skArc(sketch, "E298", {"start": v(63.05, 104.44) * mm, "mid": v(63.74, 104.02) * mm, "end": v(64.43, 103.6) * mm});
            skLineSegment(sketch, "E299", {"start": v(63.52, 99.4) * mm, "end": v(64.07, 101.66) * mm});
            skLineSegment(sketch, "E300", {"start": v(64.07, 101.66) * mm, "end": v(64.43, 103.6) * mm});
            skArc(sketch, "E301", {"start": v(63.8, 98.67) * mm, "mid": v(63.54, 99) * mm, "end": v(63.52, 99.4) * mm});
            skArc(sketch, "E302", {"start": v(63.8, 98.67) * mm, "mid": v(64, 98.54) * mm, "end": v(64.2, 98.41) * mm});
            skArc(sketch, "E303", {"start": v(64.97, 98.46) * mm, "mid": v(64.59, 98.3) * mm, "end": v(64.2, 98.41) * mm});
            skLineSegment(sketch, "E304", {"start": v(64.97, 98.46) * mm, "end": v(66.8, 99.88) * mm});
            skLineSegment(sketch, "E305", {"start": v(66.8, 99.88) * mm, "end": v(68.43, 101) * mm});
            skArc(sketch, "E306", {"start": v(68.43, 101) * mm, "mid": v(69.1, 100.54) * mm, "end": v(69.77, 100.08) * mm});
            skLineSegment(sketch, "E307", {"start": v(68.63, 95.94) * mm, "end": v(69.3, 98.17) * mm});
            skLineSegment(sketch, "E308", {"start": v(69.3, 98.17) * mm, "end": v(69.77, 100.08) * mm});
            skArc(sketch, "E309", {"start": v(68.87, 95.2) * mm, "mid": v(68.63, 95.53) * mm, "end": v(68.63, 95.94) * mm});
            skArc(sketch, "E310", {"start": v(68.87, 95.2) * mm, "mid": v(69.06, 95.06) * mm, "end": v(69.26, 94.92) * mm});
            skArc(sketch, "E311", {"start": v(70.03, 94.92) * mm, "mid": v(69.65, 94.8) * mm, "end": v(69.26, 94.92) * mm});
            skLineSegment(sketch, "E312", {"start": v(70.03, 94.92) * mm, "end": v(71.95, 96.25) * mm});
            skLineSegment(sketch, "E313", {"start": v(71.95, 96.25) * mm, "end": v(73.62, 97.28) * mm});
            skArc(sketch, "E314", {"start": v(73.62, 97.28) * mm, "mid": v(74.27, 96.79) * mm, "end": v(74.9, 96.3) * mm});
            skLineSegment(sketch, "E315", {"start": v(73.56, 92.21) * mm, "end": v(74.35, 94.4) * mm});
            skLineSegment(sketch, "E316", {"start": v(74.35, 94.4) * mm, "end": v(74.9, 96.3) * mm});
            skArc(sketch, "E317", {"start": v(73.76, 91.46) * mm, "mid": v(73.54, 91.8) * mm, "end": v(73.56, 92.21) * mm});
            skArc(sketch, "E318", {"start": v(73.76, 91.46) * mm, "mid": v(73.95, 91.31) * mm, "end": v(74.13, 91.16) * mm});
            skArc(sketch, "E319", {"start": v(74.9, 91.13) * mm, "mid": v(74.51, 91.02) * mm, "end": v(74.13, 91.16) * mm});
            skLineSegment(sketch, "E320", {"start": v(74.9, 91.13) * mm, "end": v(76.88, 92.35) * mm});
            skLineSegment(sketch, "E321", {"start": v(76.88, 92.35) * mm, "end": v(78.62, 93.3) * mm});
            skArc(sketch, "E322", {"start": v(78.62, 93.3) * mm, "mid": v(79.23, 92.77) * mm, "end": v(79.85, 92.24) * mm});
            skLineSegment(sketch, "E323", {"start": v(78.29, 88.24) * mm, "end": v(79.19, 90.38) * mm});
            skLineSegment(sketch, "E324", {"start": v(79.19, 90.38) * mm, "end": v(79.85, 92.24) * mm});
            skArc(sketch, "E325", {"start": v(78.45, 87.48) * mm, "mid": v(78.24, 87.83) * mm, "end": v(78.29, 88.24) * mm});
            skArc(sketch, "E326", {"start": v(78.45, 87.48) * mm, "mid": v(78.62, 87.32) * mm, "end": v(78.8, 87.16) * mm});
            skArc(sketch, "E327", {"start": v(79.57, 87.08) * mm, "mid": v(79.17, 87) * mm, "end": v(78.8, 87.16) * mm});
            skLineSegment(sketch, "E328", {"start": v(79.57, 87.08) * mm, "end": v(81.61, 88.2) * mm});
            skLineSegment(sketch, "E329", {"start": v(81.61, 88.2) * mm, "end": v(83.4, 89.05) * mm});
            skArc(sketch, "E330", {"start": v(83.4, 89.05) * mm, "mid": v(83.98, 88.5) * mm, "end": v(84.56, 87.94) * mm});
            skLineSegment(sketch, "E331", {"start": v(82.8, 84.02) * mm, "end": v(83.8, 86.12) * mm});
            skLineSegment(sketch, "E332", {"start": v(83.8, 86.12) * mm, "end": v(84.56, 87.94) * mm});
            skArc(sketch, "E333", {"start": v(82.92, 83.25) * mm, "mid": v(82.73, 83.62) * mm, "end": v(82.8, 84.02) * mm});
            skArc(sketch, "E334", {"start": v(82.92, 83.25) * mm, "mid": v(83.09, 83.09) * mm, "end": v(83.25, 82.92) * mm});
            skArc(sketch, "E335", {"start": v(84.02, 82.8) * mm, "mid": v(83.62, 82.73) * mm, "end": v(83.25, 82.92) * mm});
            skLineSegment(sketch, "E336", {"start": v(84.02, 82.8) * mm, "end": v(86.12, 83.8) * mm});
            skLineSegment(sketch, "E337", {"start": v(86.12, 83.8) * mm, "end": v(87.94, 84.56) * mm});
            skArc(sketch, "E338", {"start": v(87.94, 84.56) * mm, "mid": v(88.5, 83.98) * mm, "end": v(89.05, 83.4) * mm});
            skLineSegment(sketch, "E339", {"start": v(87.08, 79.57) * mm, "end": v(88.2, 81.61) * mm});
            skLineSegment(sketch, "E340", {"start": v(88.2, 81.61) * mm, "end": v(89.05, 83.4) * mm});
            skArc(sketch, "E341", {"start": v(87.16, 78.8) * mm, "mid": v(87, 79.17) * mm, "end": v(87.08, 79.57) * mm});
            skArc(sketch, "E342", {"start": v(87.16, 78.8) * mm, "mid": v(87.32, 78.62) * mm, "end": v(87.48, 78.45) * mm});
            skArc(sketch, "E343", {"start": v(88.24, 78.29) * mm, "mid": v(87.83, 78.24) * mm, "end": v(87.48, 78.45) * mm});
            skLineSegment(sketch, "E344", {"start": v(88.24, 78.29) * mm, "end": v(90.38, 79.19) * mm});
            skLineSegment(sketch, "E345", {"start": v(90.38, 79.19) * mm, "end": v(92.24, 79.85) * mm});
            skArc(sketch, "E346", {"start": v(92.24, 79.85) * mm, "mid": v(92.77, 79.23) * mm, "end": v(93.3, 78.62) * mm});
            skLineSegment(sketch, "E347", {"start": v(91.13, 74.9) * mm, "end": v(92.35, 76.88) * mm});
            skLineSegment(sketch, "E348", {"start": v(92.35, 76.88) * mm, "end": v(93.3, 78.62) * mm});
            skArc(sketch, "E349", {"start": v(91.16, 74.13) * mm, "mid": v(91.02, 74.51) * mm, "end": v(91.13, 74.9) * mm});
            skArc(sketch, "E350", {"start": v(91.16, 74.13) * mm, "mid": v(91.31, 73.95) * mm, "end": v(91.46, 73.76) * mm});
            skArc(sketch, "E351", {"start": v(92.21, 73.56) * mm, "mid": v(91.8, 73.54) * mm, "end": v(91.46, 73.76) * mm});
            skLineSegment(sketch, "E352", {"start": v(92.21, 73.56) * mm, "end": v(94.4, 74.35) * mm});
            skLineSegment(sketch, "E353", {"start": v(94.4, 74.35) * mm, "end": v(96.3, 74.9) * mm});
            skArc(sketch, "E354", {"start": v(96.3, 74.9) * mm, "mid": v(96.79, 74.27) * mm, "end": v(97.28, 73.62) * mm});
            skLineSegment(sketch, "E355", {"start": v(94.92, 70.03) * mm, "end": v(96.25, 71.95) * mm});
            skLineSegment(sketch, "E356", {"start": v(96.25, 71.95) * mm, "end": v(97.28, 73.62) * mm});
            skArc(sketch, "E357", {"start": v(94.92, 69.26) * mm, "mid": v(94.8, 69.65) * mm, "end": v(94.92, 70.03) * mm});
            skArc(sketch, "E358", {"start": v(94.92, 69.26) * mm, "mid": v(95.06, 69.06) * mm, "end": v(95.2, 68.87) * mm});
            skArc(sketch, "E359", {"start": v(95.94, 68.63) * mm, "mid": v(95.53, 68.63) * mm, "end": v(95.2, 68.87) * mm});
            skLineSegment(sketch, "E360", {"start": v(95.94, 68.63) * mm, "end": v(98.17, 69.3) * mm});
            skLineSegment(sketch, "E361", {"start": v(98.17, 69.3) * mm, "end": v(100.08, 69.77) * mm});
            skArc(sketch, "E362", {"start": v(100.08, 69.77) * mm, "mid": v(100.54, 69.1) * mm, "end": v(101, 68.43) * mm});
            skLineSegment(sketch, "E363", {"start": v(98.46, 64.97) * mm, "end": v(99.88, 66.8) * mm});
            skLineSegment(sketch, "E364", {"start": v(99.88, 66.8) * mm, "end": v(101, 68.43) * mm});
            skArc(sketch, "E365", {"start": v(98.41, 64.2) * mm, "mid": v(98.3, 64.59) * mm, "end": v(98.46, 64.97) * mm});
            skArc(sketch, "E366", {"start": v(98.41, 64.2) * mm, "mid": v(98.54, 64) * mm, "end": v(98.67, 63.8) * mm});
            skArc(sketch, "E367", {"start": v(99.4, 63.52) * mm, "mid": v(99, 63.54) * mm, "end": v(98.67, 63.8) * mm});
            skLineSegment(sketch, "E368", {"start": v(99.4, 63.52) * mm, "end": v(101.66, 64.07) * mm});
            skLineSegment(sketch, "E369", {"start": v(101.66, 64.07) * mm, "end": v(103.6, 64.43) * mm});
            skArc(sketch, "E370", {"start": v(103.6, 64.43) * mm, "mid": v(104.02, 63.74) * mm, "end": v(104.44, 63.05) * mm});
            skLineSegment(sketch, "E371", {"start": v(101.72, 59.73) * mm, "end": v(103.24, 61.5) * mm});
            skLineSegment(sketch, "E372", {"start": v(103.24, 61.5) * mm, "end": v(104.44, 63.05) * mm});
            skArc(sketch, "E373", {"start": v(101.64, 58.96) * mm, "mid": v(101.55, 59.36) * mm, "end": v(101.72, 59.73) * mm});
            skArc(sketch, "E374", {"start": v(101.64, 58.96) * mm, "mid": v(101.76, 58.75) * mm, "end": v(101.88, 58.54) * mm});
            skArc(sketch, "E375", {"start": v(102.59, 58.23) * mm, "mid": v(102.18, 58.27) * mm, "end": v(101.88, 58.54) * mm});
            skLineSegment(sketch, "E376", {"start": v(102.59, 58.23) * mm, "end": v(104.87, 58.66) * mm});
            skLineSegment(sketch, "E377", {"start": v(104.87, 58.66) * mm, "end": v(106.83, 58.92) * mm});
            skArc(sketch, "E378", {"start": v(106.83, 58.92) * mm, "mid": v(107.22, 58.21) * mm, "end": v(107.6, 57.5) * mm});
            skLineSegment(sketch, "E379", {"start": v(104.7, 54.32) * mm, "end": v(106.32, 56) * mm});
            skLineSegment(sketch, "E380", {"start": v(106.32, 56) * mm, "end": v(107.6, 57.5) * mm});
            skArc(sketch, "E381", {"start": v(104.58, 53.56) * mm, "mid": v(104.52, 53.96) * mm, "end": v(104.7, 54.32) * mm});
            skArc(sketch, "E382", {"start": v(104.58, 53.56) * mm, "mid": v(104.7, 53.34) * mm, "end": v(104.8, 53.13) * mm});
            skArc(sketch, "E383", {"start": v(105.5, 52.78) * mm, "mid": v(105.1, 52.84) * mm, "end": v(104.8, 53.13) * mm});
            skLineSegment(sketch, "E384", {"start": v(105.5, 52.78) * mm, "end": v(107.8, 53.1) * mm});
            skLineSegment(sketch, "E385", {"start": v(107.8, 53.1) * mm, "end": v(109.76, 53.25) * mm});
            skArc(sketch, "E386", {"start": v(109.76, 53.25) * mm, "mid": v(110.12, 52.52) * mm, "end": v(110.46, 51.8) * mm});
            skLineSegment(sketch, "E387", {"start": v(107.4, 48.77) * mm, "end": v(109.1, 50.36) * mm});
            skLineSegment(sketch, "E388", {"start": v(109.1, 50.36) * mm, "end": v(110.46, 51.8) * mm});
            skArc(sketch, "E389", {"start": v(107.24, 48) * mm, "mid": v(107.2, 48.42) * mm, "end": v(107.4, 48.77) * mm});
            skArc(sketch, "E390", {"start": v(107.24, 48) * mm, "mid": v(107.34, 47.8) * mm, "end": v(107.44, 47.57) * mm});
            skArc(sketch, "E391", {"start": v(108.11, 47.19) * mm, "mid": v(107.71, 47.27) * mm, "end": v(107.44, 47.57) * mm});
            skLineSegment(sketch, "E392", {"start": v(108.11, 47.19) * mm, "end": v(110.43, 47.38) * mm});
            skLineSegment(sketch, "E393", {"start": v(110.43, 47.38) * mm, "end": v(112.4, 47.43) * mm});
            skArc(sketch, "E394", {"start": v(112.4, 47.43) * mm, "mid": v(112.71, 46.69) * mm, "end": v(113.02, 45.94) * mm});
            skLineSegment(sketch, "E395", {"start": v(109.81, 43.08) * mm, "end": v(111.59, 44.58) * mm});
            skLineSegment(sketch, "E396", {"start": v(111.59, 44.58) * mm, "end": v(113.02, 45.94) * mm});
            skArc(sketch, "E397", {"start": v(109.61, 42.33) * mm, "mid": v(109.59, 42.74) * mm, "end": v(109.81, 43.08) * mm});
            skArc(sketch, "E398", {"start": v(109.61, 42.33) * mm, "mid": v(109.7, 42.1) * mm, "end": v(109.78, 41.89) * mm});
            skArc(sketch, "E399", {"start": v(110.43, 41.47) * mm, "mid": v(110.04, 41.57) * mm, "end": v(109.78, 41.89) * mm});
            skLineSegment(sketch, "E400", {"start": v(110.43, 41.47) * mm, "end": v(112.76, 41.54) * mm});
            skLineSegment(sketch, "E401", {"start": v(112.76, 41.54) * mm, "end": v(114.73, 41.49) * mm});
            skArc(sketch, "E402", {"start": v(114.73, 41.49) * mm, "mid": v(115, 40.72) * mm, "end": v(115.27, 39.96) * mm});
            skLineSegment(sketch, "E403", {"start": v(111.92, 37.27) * mm, "end": v(113.77, 38.68) * mm});
            skLineSegment(sketch, "E404", {"start": v(113.77, 38.68) * mm, "end": v(115.27, 39.96) * mm});
            skArc(sketch, "E405", {"start": v(111.68, 36.54) * mm, "mid": v(111.68, 36.94) * mm, "end": v(111.92, 37.27) * mm});
            skArc(sketch, "E406", {"start": v(111.68, 36.54) * mm, "mid": v(111.75, 36.3) * mm, "end": v(111.82, 36.08) * mm});
            skArc(sketch, "E407", {"start": v(112.45, 35.63) * mm, "mid": v(112.06, 35.75) * mm, "end": v(111.82, 36.08) * mm});
            skLineSegment(sketch, "E408", {"start": v(112.45, 35.63) * mm, "end": v(114.78, 35.58) * mm});
            skLineSegment(sketch, "E409", {"start": v(114.78, 35.58) * mm, "end": v(116.74, 35.43) * mm});
            skArc(sketch, "E410", {"start": v(116.74, 35.43) * mm, "mid": v(116.98, 34.65) * mm, "end": v(117.2, 33.87) * mm});
            skLineSegment(sketch, "E411", {"start": v(113.71, 31.36) * mm, "end": v(115.64, 32.68) * mm});
            skLineSegment(sketch, "E412", {"start": v(115.64, 32.68) * mm, "end": v(117.2, 33.87) * mm});
            skArc(sketch, "E413", {"start": v(113.43, 30.64) * mm, "mid": v(113.46, 31.05) * mm, "end": v(113.71, 31.36) * mm});
            skArc(sketch, "E414", {"start": v(113.43, 30.64) * mm, "mid": v(113.5, 30.41) * mm, "end": v(113.56, 30.18) * mm});
            skArc(sketch, "E415", {"start": v(114.16, 29.7) * mm, "mid": v(113.78, 29.84) * mm, "end": v(113.56, 30.18) * mm});
            skLineSegment(sketch, "E416", {"start": v(114.16, 29.7) * mm, "end": v(116.48, 29.52) * mm});
            skLineSegment(sketch, "E417", {"start": v(116.48, 29.52) * mm, "end": v(118.44, 29.27) * mm});
            skArc(sketch, "E418", {"start": v(118.44, 29.27) * mm, "mid": v(118.63, 28.48) * mm, "end": v(118.82, 27.7) * mm});
            skLineSegment(sketch, "E419", {"start": v(115.2, 25.37) * mm, "end": v(117.19, 26.58) * mm});
            skArc(sketch, "E420", {"start": v(110.46, -51.8) * mm, "mid": v(110.12, -52.52) * mm, "end": v(109.76, -53.25) * mm});
            skLineSegment(sketch, "E421", {"start": v(105.5, -52.78) * mm, "end": v(107.8, -53.1) * mm});
            skLineSegment(sketch, "E422", {"start": v(107.8, -53.1) * mm, "end": v(109.76, -53.25) * mm});
            skArc(sketch, "E423", {"start": v(104.8, -53.13) * mm, "mid": v(105.1, -52.84) * mm, "end": v(105.5, -52.78) * mm});
            skArc(sketch, "E424", {"start": v(104.8, -53.13) * mm, "mid": v(104.7, -53.34) * mm, "end": v(104.58, -53.56) * mm});
            skArc(sketch, "E425", {"start": v(104.7, -54.32) * mm, "mid": v(104.52, -53.96) * mm, "end": v(104.58, -53.56) * mm});
            skLineSegment(sketch, "E426", {"start": v(104.7, -54.32) * mm, "end": v(106.32, -56) * mm});
            skLineSegment(sketch, "E427", {"start": v(106.32, -56) * mm, "end": v(107.6, -57.5) * mm});
            skArc(sketch, "E428", {"start": v(107.6, -57.5) * mm, "mid": v(107.22, -58.21) * mm, "end": v(106.83, -58.92) * mm});
            skLineSegment(sketch, "E429", {"start": v(102.59, -58.23) * mm, "end": v(104.87, -58.66) * mm});
            skLineSegment(sketch, "E430", {"start": v(104.87, -58.66) * mm, "end": v(106.83, -58.92) * mm});
            skArc(sketch, "E431", {"start": v(101.88, -58.54) * mm, "mid": v(102.18, -58.27) * mm, "end": v(102.59, -58.23) * mm});
            skArc(sketch, "E432", {"start": v(101.88, -58.54) * mm, "mid": v(101.76, -58.75) * mm, "end": v(101.64, -58.96) * mm});
            skArc(sketch, "E433", {"start": v(101.72, -59.73) * mm, "mid": v(101.55, -59.36) * mm, "end": v(101.64, -58.96) * mm});
            skLineSegment(sketch, "E434", {"start": v(101.72, -59.73) * mm, "end": v(103.24, -61.5) * mm});
            skLineSegment(sketch, "E435", {"start": v(103.24, -61.5) * mm, "end": v(104.44, -63.05) * mm});
            skArc(sketch, "E436", {"start": v(104.44, -63.05) * mm, "mid": v(104.02, -63.74) * mm, "end": v(103.6, -64.43) * mm});
            skLineSegment(sketch, "E437", {"start": v(99.4, -63.52) * mm, "end": v(101.66, -64.07) * mm});
            skLineSegment(sketch, "E438", {"start": v(101.66, -64.07) * mm, "end": v(103.6, -64.43) * mm});
            skArc(sketch, "E439", {"start": v(98.67, -63.8) * mm, "mid": v(99, -63.54) * mm, "end": v(99.4, -63.52) * mm});
            skArc(sketch, "E440", {"start": v(98.67, -63.8) * mm, "mid": v(98.54, -64) * mm, "end": v(98.41, -64.2) * mm});
            skArc(sketch, "E441", {"start": v(98.46, -64.97) * mm, "mid": v(98.3, -64.59) * mm, "end": v(98.41, -64.2) * mm});
            skLineSegment(sketch, "E442", {"start": v(98.46, -64.97) * mm, "end": v(99.88, -66.8) * mm});
            skLineSegment(sketch, "E443", {"start": v(99.88, -66.8) * mm, "end": v(101, -68.43) * mm});
            skArc(sketch, "E444", {"start": v(101, -68.43) * mm, "mid": v(100.54, -69.1) * mm, "end": v(100.08, -69.77) * mm});
            skLineSegment(sketch, "E445", {"start": v(95.94, -68.63) * mm, "end": v(98.17, -69.3) * mm});
            skLineSegment(sketch, "E446", {"start": v(98.17, -69.3) * mm, "end": v(100.08, -69.77) * mm});
            skArc(sketch, "E447", {"start": v(95.2, -68.87) * mm, "mid": v(95.53, -68.63) * mm, "end": v(95.94, -68.63) * mm});
            skArc(sketch, "E448", {"start": v(95.2, -68.87) * mm, "mid": v(95.06, -69.06) * mm, "end": v(94.92, -69.26) * mm});
            skArc(sketch, "E449", {"start": v(94.92, -70.03) * mm, "mid": v(94.8, -69.65) * mm, "end": v(94.92, -69.26) * mm});
            skLineSegment(sketch, "E450", {"start": v(94.92, -70.03) * mm, "end": v(96.25, -71.95) * mm});
            skLineSegment(sketch, "E451", {"start": v(96.25, -71.95) * mm, "end": v(97.28, -73.62) * mm});
            skArc(sketch, "E452", {"start": v(97.28, -73.62) * mm, "mid": v(96.79, -74.27) * mm, "end": v(96.3, -74.9) * mm});
            skLineSegment(sketch, "E453", {"start": v(92.21, -73.56) * mm, "end": v(94.4, -74.35) * mm});
            skLineSegment(sketch, "E454", {"start": v(94.4, -74.35) * mm, "end": v(96.3, -74.9) * mm});
            skArc(sketch, "E455", {"start": v(91.46, -73.76) * mm, "mid": v(91.8, -73.54) * mm, "end": v(92.21, -73.56) * mm});
            skArc(sketch, "E456", {"start": v(91.46, -73.76) * mm, "mid": v(91.31, -73.95) * mm, "end": v(91.16, -74.13) * mm});
            skArc(sketch, "E457", {"start": v(91.13, -74.9) * mm, "mid": v(91.02, -74.51) * mm, "end": v(91.16, -74.13) * mm});
            skLineSegment(sketch, "E458", {"start": v(91.13, -74.9) * mm, "end": v(92.35, -76.88) * mm});
            skLineSegment(sketch, "E459", {"start": v(92.35, -76.88) * mm, "end": v(93.3, -78.62) * mm});
            skArc(sketch, "E460", {"start": v(93.3, -78.62) * mm, "mid": v(92.77, -79.23) * mm, "end": v(92.24, -79.85) * mm});
            skLineSegment(sketch, "E461", {"start": v(88.24, -78.29) * mm, "end": v(90.38, -79.19) * mm});
            skLineSegment(sketch, "E462", {"start": v(90.38, -79.19) * mm, "end": v(92.24, -79.85) * mm});
            skArc(sketch, "E463", {"start": v(87.48, -78.45) * mm, "mid": v(87.83, -78.24) * mm, "end": v(88.24, -78.29) * mm});
            skArc(sketch, "E464", {"start": v(87.48, -78.45) * mm, "mid": v(87.32, -78.62) * mm, "end": v(87.16, -78.8) * mm});
            skArc(sketch, "E465", {"start": v(87.08, -79.57) * mm, "mid": v(87, -79.17) * mm, "end": v(87.16, -78.8) * mm});
            skLineSegment(sketch, "E466", {"start": v(87.08, -79.57) * mm, "end": v(88.2, -81.61) * mm});
            skLineSegment(sketch, "E467", {"start": v(88.2, -81.61) * mm, "end": v(89.05, -83.4) * mm});
            skArc(sketch, "E468", {"start": v(89.05, -83.4) * mm, "mid": v(88.5, -83.98) * mm, "end": v(87.94, -84.56) * mm});
            skLineSegment(sketch, "E469", {"start": v(84.02, -82.8) * mm, "end": v(86.12, -83.8) * mm});
            skLineSegment(sketch, "E470", {"start": v(71.95, -96.25) * mm, "end": v(73.62, -97.28) * mm});
            skArc(sketch, "E471", {"start": v(69.26, -94.92) * mm, "mid": v(69.65, -94.8) * mm, "end": v(70.03, -94.92) * mm});
            skArc(sketch, "E472", {"start": v(69.26, -94.92) * mm, "mid": v(69.06, -95.06) * mm, "end": v(68.87, -95.2) * mm});
            skArc(sketch, "E473", {"start": v(68.63, -95.94) * mm, "mid": v(68.63, -95.53) * mm, "end": v(68.87, -95.2) * mm});
            skLineSegment(sketch, "E474", {"start": v(68.63, -95.94) * mm, "end": v(69.3, -98.17) * mm});
            skLineSegment(sketch, "E475", {"start": v(69.3, -98.17) * mm, "end": v(69.77, -100.08) * mm});
            skArc(sketch, "E476", {"start": v(69.77, -100.08) * mm, "mid": v(69.1, -100.54) * mm, "end": v(68.43, -101) * mm});
            skLineSegment(sketch, "E477", {"start": v(64.97, -98.46) * mm, "end": v(66.8, -99.88) * mm});
            skLineSegment(sketch, "E478", {"start": v(66.8, -99.88) * mm, "end": v(68.43, -101) * mm});
            skArc(sketch, "E479", {"start": v(64.2, -98.41) * mm, "mid": v(64.59, -98.3) * mm, "end": v(64.97, -98.46) * mm});
            skArc(sketch, "E480", {"start": v(64.2, -98.41) * mm, "mid": v(64, -98.54) * mm, "end": v(63.8, -98.67) * mm});
            skArc(sketch, "E481", {"start": v(63.52, -99.4) * mm, "mid": v(63.54, -99) * mm, "end": v(63.8, -98.67) * mm});
            skArc(sketch, "E482", {"start": v(58.96, -101.64) * mm, "mid": v(58.75, -101.76) * mm, "end": v(58.54, -101.88) * mm});
            skArc(sketch, "E483", {"start": v(58.23, -102.59) * mm, "mid": v(58.27, -102.18) * mm, "end": v(58.54, -101.88) * mm});
            skLineSegment(sketch, "E484", {"start": v(58.23, -102.59) * mm, "end": v(58.66, -104.87) * mm});
            skLineSegment(sketch, "E485", {"start": v(58.66, -104.87) * mm, "end": v(58.92, -106.83) * mm});
            skArc(sketch, "E486", {"start": v(58.96, -101.64) * mm, "mid": v(59.36, -101.55) * mm, "end": v(59.73, -101.72) * mm});
            skLineSegment(sketch, "E487", {"start": v(61.5, -103.24) * mm, "end": v(63.05, -104.44) * mm});
            skLineSegment(sketch, "E488", {"start": v(59.73, -101.72) * mm, "end": v(61.5, -103.24) * mm});
            skArc(sketch, "E489", {"start": v(64.43, -103.6) * mm, "mid": v(63.74, -104.02) * mm, "end": v(63.05, -104.44) * mm});
            skLineSegment(sketch, "E490", {"start": v(64.07, -101.66) * mm, "end": v(64.43, -103.6) * mm});
            skLineSegment(sketch, "E491", {"start": v(63.52, -99.4) * mm, "end": v(64.07, -101.66) * mm});
            skLineSegment(sketch, "E492", {"start": v(70.03, -94.92) * mm, "end": v(71.95, -96.25) * mm});
            skArc(sketch, "E493", {"start": v(74.9, -96.3) * mm, "mid": v(74.27, -96.79) * mm, "end": v(73.62, -97.28) * mm});
            skLineSegment(sketch, "E494", {"start": v(74.35, -94.4) * mm, "end": v(74.9, -96.3) * mm});
            skLineSegment(sketch, "E495", {"start": v(73.56, -92.21) * mm, "end": v(74.35, -94.4) * mm});
            skArc(sketch, "E496", {"start": v(73.56, -92.21) * mm, "mid": v(73.54, -91.8) * mm, "end": v(73.76, -91.46) * mm});
            skArc(sketch, "E497", {"start": v(74.13, -91.16) * mm, "mid": v(73.95, -91.31) * mm, "end": v(73.76, -91.46) * mm});
            skArc(sketch, "E498", {"start": v(74.13, -91.16) * mm, "mid": v(74.51, -91.02) * mm, "end": v(74.9, -91.13) * mm});
            skLineSegment(sketch, "E499", {"start": v(76.88, -92.35) * mm, "end": v(78.62, -93.3) * mm});
            skLineSegment(sketch, "E500", {"start": v(74.9, -91.13) * mm, "end": v(76.88, -92.35) * mm});
            skArc(sketch, "E501", {"start": v(79.85, -92.24) * mm, "mid": v(79.23, -92.77) * mm, "end": v(78.62, -93.3) * mm});
            skLineSegment(sketch, "E502", {"start": v(79.19, -90.38) * mm, "end": v(79.85, -92.24) * mm});
            skLineSegment(sketch, "E503", {"start": v(78.29, -88.24) * mm, "end": v(79.19, -90.38) * mm});
            skArc(sketch, "E504", {"start": v(78.29, -88.24) * mm, "mid": v(78.24, -87.83) * mm, "end": v(78.45, -87.48) * mm});
            skArc(sketch, "E505", {"start": v(78.8, -87.16) * mm, "mid": v(78.62, -87.32) * mm, "end": v(78.45, -87.48) * mm});
            skArc(sketch, "E506", {"start": v(78.8, -87.16) * mm, "mid": v(79.17, -87) * mm, "end": v(79.57, -87.08) * mm});
            skLineSegment(sketch, "E507", {"start": v(81.61, -88.2) * mm, "end": v(83.4, -89.05) * mm});
            skLineSegment(sketch, "E508", {"start": v(79.57, -87.08) * mm, "end": v(81.61, -88.2) * mm});
            skArc(sketch, "E509", {"start": v(84.56, -87.94) * mm, "mid": v(83.98, -88.5) * mm, "end": v(83.4, -89.05) * mm});
            skLineSegment(sketch, "E510", {"start": v(83.8, -86.12) * mm, "end": v(84.56, -87.94) * mm});
            skLineSegment(sketch, "E511", {"start": v(82.8, -84.02) * mm, "end": v(83.8, -86.12) * mm});
            skArc(sketch, "E512", {"start": v(82.8, -84.02) * mm, "mid": v(82.73, -83.62) * mm, "end": v(82.92, -83.25) * mm});
            skArc(sketch, "E513", {"start": v(83.25, -82.92) * mm, "mid": v(83.09, -83.09) * mm, "end": v(82.92, -83.25) * mm});
            skArc(sketch, "E514", {"start": v(83.25, -82.92) * mm, "mid": v(83.62, -82.73) * mm, "end": v(84.02, -82.8) * mm});
            skLineSegment(sketch, "E515", {"start": v(86.12, -83.8) * mm, "end": v(87.94, -84.56) * mm});
            skLineSegment(sketch, "E516", {"start": v(109.1, -50.36) * mm, "end": v(110.46, -51.8) * mm});
            skLineSegment(sketch, "E517", {"start": v(107.4, -48.77) * mm, "end": v(109.1, -50.36) * mm});
            skArc(sketch, "E518", {"start": v(107.4, -48.77) * mm, "mid": v(107.2, -48.42) * mm, "end": v(107.24, -48) * mm});
            skArc(sketch, "E519", {"start": v(107.44, -47.57) * mm, "mid": v(107.34, -47.8) * mm, "end": v(107.24, -48) * mm});
            skArc(sketch, "E520", {"start": v(107.44, -47.57) * mm, "mid": v(107.71, -47.27) * mm, "end": v(108.11, -47.19) * mm});
            skLineSegment(sketch, "E521", {"start": v(110.43, -47.38) * mm, "end": v(112.4, -47.43) * mm});
            skLineSegment(sketch, "E522", {"start": v(108.11, -47.19) * mm, "end": v(110.43, -47.38) * mm});
            skArc(sketch, "E523", {"start": v(113.02, -45.94) * mm, "mid": v(112.71, -46.69) * mm, "end": v(112.4, -47.43) * mm});
            skLineSegment(sketch, "E524", {"start": v(111.59, -44.58) * mm, "end": v(113.02, -45.94) * mm});
            skLineSegment(sketch, "E525", {"start": v(109.81, -43.08) * mm, "end": v(111.59, -44.58) * mm});
            skArc(sketch, "E526", {"start": v(109.81, -43.08) * mm, "mid": v(109.59, -42.74) * mm, "end": v(109.61, -42.33) * mm});
            skArc(sketch, "E527", {"start": v(109.78, -41.89) * mm, "mid": v(109.7, -42.1) * mm, "end": v(109.61, -42.33) * mm});
            skArc(sketch, "E528", {"start": v(109.78, -41.89) * mm, "mid": v(110.04, -41.57) * mm, "end": v(110.43, -41.47) * mm});
            skLineSegment(sketch, "E529", {"start": v(112.76, -41.54) * mm, "end": v(114.73, -41.49) * mm});
            skLineSegment(sketch, "E530", {"start": v(110.43, -41.47) * mm, "end": v(112.76, -41.54) * mm});
            skArc(sketch, "E531", {"start": v(115.27, -39.96) * mm, "mid": v(115, -40.72) * mm, "end": v(114.73, -41.49) * mm});
            skLineSegment(sketch, "E532", {"start": v(113.77, -38.68) * mm, "end": v(115.27, -39.96) * mm});
            skLineSegment(sketch, "E533", {"start": v(111.92, -37.27) * mm, "end": v(113.77, -38.68) * mm});
            skArc(sketch, "E534", {"start": v(111.92, -37.27) * mm, "mid": v(111.68, -36.94) * mm, "end": v(111.68, -36.54) * mm});
            skArc(sketch, "E535", {"start": v(111.82, -36.08) * mm, "mid": v(111.75, -36.3) * mm, "end": v(111.68, -36.54) * mm});
            skArc(sketch, "E536", {"start": v(111.82, -36.08) * mm, "mid": v(112.06, -35.75) * mm, "end": v(112.45, -35.63) * mm});
            skLineSegment(sketch, "E537", {"start": v(114.78, -35.58) * mm, "end": v(116.74, -35.43) * mm});
            skLineSegment(sketch, "E538", {"start": v(112.45, -35.63) * mm, "end": v(114.78, -35.58) * mm});
            skArc(sketch, "E539", {"start": v(117.2, -33.87) * mm, "mid": v(116.98, -34.65) * mm, "end": v(116.74, -35.43) * mm});
            skLineSegment(sketch, "E540", {"start": v(115.64, -32.68) * mm, "end": v(117.2, -33.87) * mm});
            skLineSegment(sketch, "E541", {"start": v(113.71, -31.36) * mm, "end": v(115.64, -32.68) * mm});
            skArc(sketch, "E542", {"start": v(113.71, -31.36) * mm, "mid": v(113.46, -31.05) * mm, "end": v(113.43, -30.64) * mm});
            skArc(sketch, "E543", {"start": v(113.56, -30.18) * mm, "mid": v(113.5, -30.41) * mm, "end": v(113.43, -30.64) * mm});
            skArc(sketch, "E544", {"start": v(113.56, -30.18) * mm, "mid": v(113.78, -29.84) * mm, "end": v(114.16, -29.7) * mm});
            skLineSegment(sketch, "E545", {"start": v(116.48, -29.52) * mm, "end": v(118.44, -29.27) * mm});
            skLineSegment(sketch, "E546", {"start": v(114.16, -29.7) * mm, "end": v(116.48, -29.52) * mm});
            skArc(sketch, "E547", {"start": v(118.82, -27.7) * mm, "mid": v(118.63, -28.48) * mm, "end": v(118.44, -29.27) * mm});
            skLineSegment(sketch, "E548", {"start": v(117.19, -26.58) * mm, "end": v(118.82, -27.7) * mm});
            skLineSegment(sketch, "E549", {"start": v(115.2, -25.37) * mm, "end": v(117.19, -26.58) * mm});
            skArc(sketch, "E550", {"start": v(115.2, -25.37) * mm, "mid": v(114.93, -25.07) * mm, "end": v(114.88, -24.66) * mm});
            skArc(sketch, "E551", {"start": v(114.98, -24.2) * mm, "mid": v(114.93, -24.43) * mm, "end": v(114.88, -24.66) * mm});
            skArc(sketch, "E552", {"start": v(114.98, -24.2) * mm, "mid": v(115.19, -23.84) * mm, "end": v(115.56, -23.68) * mm});
            skLineSegment(sketch, "E553", {"start": v(117.87, -23.38) * mm, "end": v(119.8, -23.03) * mm});
            skLineSegment(sketch, "E554", {"start": v(115.56, -23.68) * mm, "end": v(117.87, -23.38) * mm});
            skArc(sketch, "E555", {"start": v(120.1, -21.44) * mm, "mid": v(119.96, -22.23) * mm, "end": v(119.8, -23.03) * mm});
            skLineSegment(sketch, "E556", {"start": v(118.42, -20.4) * mm, "end": v(120.1, -21.44) * mm});
            skLineSegment(sketch, "E557", {"start": v(116.37, -19.3) * mm, "end": v(118.42, -20.4) * mm});
            skArc(sketch, "E558", {"start": v(116.37, -19.3) * mm, "mid": v(116.08, -19.02) * mm, "end": v(116.02, -18.62) * mm});
            skArc(sketch, "E559", {"start": v(116.1, -18.15) * mm, "mid": v(116.05, -18.38) * mm, "end": v(116.02, -18.62) * mm});
            skArc(sketch, "E560", {"start": v(116.1, -18.15) * mm, "mid": v(116.28, -17.78) * mm, "end": v(116.64, -17.6) * mm});
            skLineSegment(sketch, "E561", {"start": v(118.93, -17.18) * mm, "end": v(120.85, -16.73) * mm});
            skLineSegment(sketch, "E562", {"start": v(116.64, -17.6) * mm, "end": v(118.93, -17.18) * mm});
            skArc(sketch, "E563", {"start": v(121.06, -15.12) * mm, "mid": v(120.96, -15.92) * mm, "end": v(120.85, -16.73) * mm});
            skLineSegment(sketch, "E564", {"start": v(119.33, -14.18) * mm, "end": v(121.06, -15.12) * mm});
            skLineSegment(sketch, "E565", {"start": v(117.22, -13.19) * mm, "end": v(119.33, -14.18) * mm});
            skArc(sketch, "E566", {"start": v(117.22, -13.19) * mm, "mid": v(116.92, -12.92) * mm, "end": v(116.83, -12.52) * mm});
            skArc(sketch, "E567", {"start": v(116.88, -12.05) * mm, "mid": v(116.86, -12.28) * mm, "end": v(116.83, -12.52) * mm});
            skArc(sketch, "E568", {"start": v(116.88, -12.05) * mm, "mid": v(117.05, -11.67) * mm, "end": v(117.4, -11.47) * mm});
            skLineSegment(sketch, "E569", {"start": v(119.67, -10.94) * mm, "end": v(121.56, -10.38) * mm});
            skLineSegment(sketch, "E570", {"start": v(117.4, -11.47) * mm, "end": v(119.67, -10.94) * mm});
            skArc(sketch, "E571", {"start": v(121.68, -8.76) * mm, "mid": v(121.62, -9.57) * mm, "end": v(121.56, -10.38) * mm});
            skLineSegment(sketch, "E572", {"start": v(119.9, -7.92) * mm, "end": v(121.68, -8.76) * mm});
            skLineSegment(sketch, "E573", {"start": v(117.75, -7.04) * mm, "end": v(119.9, -7.92) * mm});
            skArc(sketch, "E574", {"start": v(117.75, -7.04) * mm, "mid": v(117.43, -6.78) * mm, "end": v(117.33, -6.39) * mm});
            skArc(sketch, "E575", {"start": v(117.35, -5.91) * mm, "mid": v(117.34, -6.15) * mm, "end": v(117.33, -6.39) * mm});
            skArc(sketch, "E576", {"start": v(117.35, -5.91) * mm, "mid": v(117.5, -5.53) * mm, "end": v(117.84, -5.3) * mm});
            skLineSegment(sketch, "E577", {"start": v(120.08, -4.66) * mm, "end": v(121.93, -4) * mm});
            skLineSegment(sketch, "E578", {"start": v(117.84, -5.3) * mm, "end": v(120.08, -4.66) * mm});
            skArc(sketch, "E579", {"start": v(121.98, -2.38) * mm, "mid": v(121.96, -3.2) * mm, "end": v(121.93, -4) * mm});
            skLineSegment(sketch, "E580", {"start": v(120.15, -1.63) * mm, "end": v(121.98, -2.38) * mm});
            skLineSegment(sketch, "E581", {"start": v(117.96, -0.86) * mm, "end": v(120.15, -1.63) * mm});
            skArc(sketch, "E582", {"start": v(117.96, -0.86) * mm, "mid": v(117.63, -0.63) * mm, "end": v(117.5, -0.24) * mm});
            skArc(sketch, "E583", {"start": v(117.5, 0.24) * mm, "mid": v(117.5, 0) * mm, "end": v(117.5, -0.24) * mm});
            skArc(sketch, "E584", {"start": v(117.5, 0.24) * mm, "mid": v(117.63, 0.63) * mm, "end": v(117.96, 0.86) * mm});
            skLineSegment(sketch, "E585", {"start": v(120.15, 1.63) * mm, "end": v(121.98, 2.38) * mm});
            skLineSegment(sketch, "E586", {"start": v(117.96, 0.86) * mm, "end": v(120.15, 1.63) * mm});
            skArc(sketch, "E587", {"start": v(121.93, 4) * mm, "mid": v(121.96, 3.2) * mm, "end": v(121.98, 2.38) * mm});
            skLineSegment(sketch, "E588", {"start": v(120.08, 4.66) * mm, "end": v(121.93, 4) * mm});
            skLineSegment(sketch, "E589", {"start": v(117.84, 5.3) * mm, "end": v(120.08, 4.66) * mm});
            skArc(sketch, "E590", {"start": v(117.84, 5.3) * mm, "mid": v(117.5, 5.53) * mm, "end": v(117.35, 5.91) * mm});
            skArc(sketch, "E591", {"start": v(117.33, 6.39) * mm, "mid": v(117.34, 6.15) * mm, "end": v(117.35, 5.91) * mm});
            skArc(sketch, "E592", {"start": v(117.33, 6.39) * mm, "mid": v(117.43, 6.78) * mm, "end": v(117.75, 7.04) * mm});
            skLineSegment(sketch, "E593", {"start": v(119.9, 7.92) * mm, "end": v(121.68, 8.76) * mm});
            skLineSegment(sketch, "E594", {"start": v(117.75, 7.04) * mm, "end": v(119.9, 7.92) * mm});
            skArc(sketch, "E595", {"start": v(121.56, 10.38) * mm, "mid": v(121.62, 9.57) * mm, "end": v(121.68, 8.76) * mm});
            skLineSegment(sketch, "E596", {"start": v(119.67, 10.94) * mm, "end": v(121.56, 10.38) * mm});
            skLineSegment(sketch, "E597", {"start": v(117.4, 11.47) * mm, "end": v(119.67, 10.94) * mm});
            skArc(sketch, "E598", {"start": v(117.4, 11.47) * mm, "mid": v(117.05, 11.67) * mm, "end": v(116.88, 12.05) * mm});
            skArc(sketch, "E599", {"start": v(116.83, 12.52) * mm, "mid": v(116.86, 12.28) * mm, "end": v(116.88, 12.05) * mm});
            skArc(sketch, "E600", {"start": v(116.83, 12.52) * mm, "mid": v(116.92, 12.92) * mm, "end": v(117.22, 13.19) * mm});
            skLineSegment(sketch, "E601", {"start": v(119.33, 14.18) * mm, "end": v(121.06, 15.12) * mm});
            skLineSegment(sketch, "E602", {"start": v(117.22, 13.19) * mm, "end": v(119.33, 14.18) * mm});
            skArc(sketch, "E603", {"start": v(120.85, 16.73) * mm, "mid": v(120.96, 15.92) * mm, "end": v(121.06, 15.12) * mm});
            skLineSegment(sketch, "E604", {"start": v(118.93, 17.18) * mm, "end": v(120.85, 16.73) * mm});
            skLineSegment(sketch, "E605", {"start": v(116.64, 17.6) * mm, "end": v(118.93, 17.18) * mm});
            skArc(sketch, "E606", {"start": v(116.64, 17.6) * mm, "mid": v(116.28, 17.78) * mm, "end": v(116.1, 18.15) * mm});
            skArc(sketch, "E607", {"start": v(116.02, 18.62) * mm, "mid": v(116.05, 18.38) * mm, "end": v(116.1, 18.15) * mm});
            skArc(sketch, "E608", {"start": v(116.02, 18.62) * mm, "mid": v(116.08, 19.02) * mm, "end": v(116.37, 19.3) * mm});
            skLineSegment(sketch, "E609", {"start": v(118.42, 20.4) * mm, "end": v(120.1, 21.44) * mm});
            skLineSegment(sketch, "E610", {"start": v(116.37, 19.3) * mm, "end": v(118.42, 20.4) * mm});
            skArc(sketch, "E611", {"start": v(119.8, 23.03) * mm, "mid": v(119.96, 22.23) * mm, "end": v(120.1, 21.44) * mm});
            skLineSegment(sketch, "E612", {"start": v(117.87, 23.38) * mm, "end": v(119.8, 23.03) * mm});
            skLineSegment(sketch, "E613", {"start": v(115.56, 23.68) * mm, "end": v(117.87, 23.38) * mm});
            skArc(sketch, "E614", {"start": v(115.56, 23.68) * mm, "mid": v(115.19, 23.84) * mm, "end": v(114.98, 24.2) * mm});
            skArc(sketch, "E615", {"start": v(114.88, 24.66) * mm, "mid": v(114.93, 24.43) * mm, "end": v(114.98, 24.2) * mm});
            skArc(sketch, "E616", {"start": v(114.88, 24.66) * mm, "mid": v(114.93, 25.07) * mm, "end": v(115.2, 25.37) * mm});
            skLineSegment(sketch, "E617", {"start": v(117.19, 26.58) * mm, "end": v(118.82, 27.7) * mm});
            skLineSegment(sketch, "E618", {"start": v(0, -2.9) * mm, "end": v(0, -3.1) * mm});
            skArc(sketch, "E619", {"start": v(0, -2.9) * mm, "mid": v(-0.75, -2.8) * mm, "end": v(-1.45, -2.51) * mm});
            skLineSegment(sketch, "E620", {"start": v(-1.45, -2.51) * mm, "end": v(-1.55, -2.68) * mm});
            skLineSegment(sketch, "E621", {"start": v(-24.1, 25.54) * mm, "end": v(-63.56, 49.73) * mm});
            skArc(sketch, "E622", {"start": v(-63.56, 49.73) * mm, "mid": v(-67.31, 55.52) * mm, "end": v(-65.17, 62.07) * mm});
            skArc(sketch, "E623", {"start": v(-65.17, 62.07) * mm, "mid": v(-44.1, 78.45) * mm, "end": v(-19.16, 87.94) * mm});
            skArc(sketch, "E624", {"start": v(-19.16, 87.94) * mm, "mid": v(-12.35, 86.28) * mm, "end": v(-9.46, 79.91) * mm});
            skLineSegment(sketch, "E625", {"start": v(-10.7, 32.88) * mm, "end": v(-9.46, 79.91) * mm});
            skArc(sketch, "E626", {"start": v(-10.7, 32.88) * mm, "mid": v(-11.83, 28.96) * mm, "end": v(-14.75, 26.12) * mm});
            skArc(sketch, "E627", {"start": v(-15.72, 25.55) * mm, "mid": v(-15.24, 25.84) * mm, "end": v(-14.75, 26.12) * mm});
            skArc(sketch, "E628", {"start": v(-15.72, 25.55) * mm, "mid": v(-19.9, 24.37) * mm, "end": v(-24.1, 25.54) * mm});
            skArc(sketch, "E629", {"start": v(63.9, -63.38) * mm, "mid": v(41.77, -79.72) * mm, "end": v(15.74, -88.61) * mm});
            skArc(sketch, "E630", {"start": v(15.74, -88.61) * mm, "mid": v(9.12, -86.8) * mm, "end": v(6.34, -80.53) * mm});
            skLineSegment(sketch, "E631", {"start": v(7.55, -34.46) * mm, "end": v(6.34, -80.53) * mm});
            skArc(sketch, "E632", {"start": v(7.55, -34.46) * mm, "mid": v(8.89, -30.24) * mm, "end": v(12.27, -27.37) * mm});
            skArc(sketch, "E633", {"start": v(14.47, -26.28) * mm, "mid": v(13.38, -26.85) * mm, "end": v(12.27, -27.37) * mm});
            skArc(sketch, "E634", {"start": v(14.47, -26.28) * mm, "mid": v(18.5, -25.3) * mm, "end": v(22.5, -26.47) * mm});
            skLineSegment(sketch, "E635", {"start": v(22.5, -26.47) * mm, "end": v(62.4, -50.92) * mm});
            skArc(sketch, "E636", {"start": v(62.4, -50.92) * mm, "mid": v(66.16, -56.79) * mm, "end": v(63.9, -63.38) * mm});
            skArc(sketch, "E637", {"start": v(58.92, -106.83) * mm, "mid": v(58.21, -107.22) * mm, "end": v(57.5, -107.6) * mm});
            skLineSegment(sketch, "E638", {"start": v(54.32, -104.7) * mm, "end": v(56, -106.32) * mm});
            skLineSegment(sketch, "E639", {"start": v(56, -106.32) * mm, "end": v(57.5, -107.6) * mm});
            skArc(sketch, "E640", {"start": v(53.56, -104.58) * mm, "mid": v(53.96, -104.52) * mm, "end": v(54.32, -104.7) * mm});
            skArc(sketch, "E641", {"start": v(53.56, -104.58) * mm, "mid": v(53.34, -104.7) * mm, "end": v(53.13, -104.8) * mm});
            skArc(sketch, "E642", {"start": v(52.78, -105.5) * mm, "mid": v(52.84, -105.1) * mm, "end": v(53.13, -104.8) * mm});
            skLineSegment(sketch, "E643", {"start": v(52.78, -105.5) * mm, "end": v(53.1, -107.8) * mm});
            skLineSegment(sketch, "E644", {"start": v(53.1, -107.8) * mm, "end": v(53.25, -109.76) * mm});
            skArc(sketch, "E645", {"start": v(53.25, -109.76) * mm, "mid": v(52.52, -110.12) * mm, "end": v(51.8, -110.46) * mm});
            skLineSegment(sketch, "E646", {"start": v(48.77, -107.4) * mm, "end": v(50.36, -109.1) * mm});
            skLineSegment(sketch, "E647", {"start": v(50.36, -109.1) * mm, "end": v(51.8, -110.46) * mm});
            skArc(sketch, "E648", {"start": v(48, -107.24) * mm, "mid": v(48.42, -107.2) * mm, "end": v(48.77, -107.4) * mm});
            skArc(sketch, "E649", {"start": v(48, -107.24) * mm, "mid": v(47.8, -107.34) * mm, "end": v(47.57, -107.44) * mm});
            skArc(sketch, "E650", {"start": v(47.19, -108.11) * mm, "mid": v(47.27, -107.71) * mm, "end": v(47.57, -107.44) * mm});
            skLineSegment(sketch, "E651", {"start": v(47.19, -108.11) * mm, "end": v(47.38, -110.43) * mm});
            skLineSegment(sketch, "E652", {"start": v(47.38, -110.43) * mm, "end": v(47.43, -112.4) * mm});
            skArc(sketch, "E653", {"start": v(47.43, -112.4) * mm, "mid": v(46.69, -112.71) * mm, "end": v(45.94, -113.02) * mm});
            skLineSegment(sketch, "E654", {"start": v(43.08, -109.81) * mm, "end": v(44.58, -111.59) * mm});
            skLineSegment(sketch, "E655", {"start": v(44.58, -111.59) * mm, "end": v(45.94, -113.02) * mm});
            skArc(sketch, "E656", {"start": v(42.33, -109.61) * mm, "mid": v(42.74, -109.59) * mm, "end": v(43.08, -109.81) * mm});
            skArc(sketch, "E657", {"start": v(42.33, -109.61) * mm, "mid": v(42.1, -109.7) * mm, "end": v(41.89, -109.78) * mm});
            skArc(sketch, "E658", {"start": v(41.47, -110.43) * mm, "mid": v(41.57, -110.04) * mm, "end": v(41.89, -109.78) * mm});
            skLineSegment(sketch, "E659", {"start": v(41.47, -110.43) * mm, "end": v(41.54, -112.76) * mm});
            skLineSegment(sketch, "E660", {"start": v(41.54, -112.76) * mm, "end": v(41.49, -114.73) * mm});
            skArc(sketch, "E661", {"start": v(41.49, -114.73) * mm, "mid": v(40.72, -115) * mm, "end": v(39.96, -115.27) * mm});
            skLineSegment(sketch, "E662", {"start": v(37.27, -111.92) * mm, "end": v(38.68, -113.77) * mm});
            skLineSegment(sketch, "E663", {"start": v(38.68, -113.77) * mm, "end": v(39.96, -115.27) * mm});
            skArc(sketch, "E664", {"start": v(36.54, -111.68) * mm, "mid": v(36.94, -111.68) * mm, "end": v(37.27, -111.92) * mm});
            skArc(sketch, "E665", {"start": v(36.54, -111.68) * mm, "mid": v(36.3, -111.75) * mm, "end": v(36.08, -111.82) * mm});
            skArc(sketch, "E666", {"start": v(35.63, -112.45) * mm, "mid": v(35.75, -112.06) * mm, "end": v(36.08, -111.82) * mm});
            skLineSegment(sketch, "E667", {"start": v(35.63, -112.45) * mm, "end": v(35.58, -114.78) * mm});
            skLineSegment(sketch, "E668", {"start": v(35.58, -114.78) * mm, "end": v(35.43, -116.74) * mm});
            skArc(sketch, "E669", {"start": v(35.43, -116.74) * mm, "mid": v(34.65, -116.98) * mm, "end": v(33.87, -117.2) * mm});
            skLineSegment(sketch, "E670", {"start": v(31.36, -113.71) * mm, "end": v(32.68, -115.64) * mm});
            skLineSegment(sketch, "E671", {"start": v(32.68, -115.64) * mm, "end": v(33.87, -117.2) * mm});
            skArc(sketch, "E672", {"start": v(30.64, -113.43) * mm, "mid": v(31.05, -113.46) * mm, "end": v(31.36, -113.71) * mm});
            skArc(sketch, "E673", {"start": v(30.64, -113.43) * mm, "mid": v(30.41, -113.5) * mm, "end": v(30.18, -113.56) * mm});
            skArc(sketch, "E674", {"start": v(29.7, -114.16) * mm, "mid": v(29.84, -113.78) * mm, "end": v(30.18, -113.56) * mm});
            skLineSegment(sketch, "E675", {"start": v(29.7, -114.16) * mm, "end": v(29.52, -116.48) * mm});
            skLineSegment(sketch, "E676", {"start": v(29.52, -116.48) * mm, "end": v(29.27, -118.44) * mm});
            skArc(sketch, "E677", {"start": v(29.27, -118.44) * mm, "mid": v(28.48, -118.63) * mm, "end": v(27.7, -118.82) * mm});
            skLineSegment(sketch, "E678", {"start": v(25.37, -115.2) * mm, "end": v(26.58, -117.19) * mm});
            skLineSegment(sketch, "E679", {"start": v(26.58, -117.19) * mm, "end": v(27.7, -118.82) * mm});
            skArc(sketch, "E680", {"start": v(24.66, -114.88) * mm, "mid": v(25.07, -114.93) * mm, "end": v(25.37, -115.2) * mm});
            skArc(sketch, "E681", {"start": v(24.66, -114.88) * mm, "mid": v(24.43, -114.93) * mm, "end": v(24.2, -114.98) * mm});
            skArc(sketch, "E682", {"start": v(23.68, -115.56) * mm, "mid": v(23.84, -115.19) * mm, "end": v(24.2, -114.98) * mm});
            skLineSegment(sketch, "E683", {"start": v(23.68, -115.56) * mm, "end": v(23.38, -117.87) * mm});
            skLineSegment(sketch, "E684", {"start": v(23.38, -117.87) * mm, "end": v(23.03, -119.8) * mm});
            skArc(sketch, "E685", {"start": v(23.03, -119.8) * mm, "mid": v(22.23, -119.96) * mm, "end": v(21.44, -120.1) * mm});
            skLineSegment(sketch, "E686", {"start": v(19.3, -116.37) * mm, "end": v(20.4, -118.42) * mm});
            skLineSegment(sketch, "E687", {"start": v(20.4, -118.42) * mm, "end": v(21.44, -120.1) * mm});
            skArc(sketch, "E688", {"start": v(18.62, -116.02) * mm, "mid": v(19.02, -116.08) * mm, "end": v(19.3, -116.37) * mm});
            skArc(sketch, "E689", {"start": v(18.62, -116.02) * mm, "mid": v(18.38, -116.05) * mm, "end": v(18.15, -116.1) * mm});
            skArc(sketch, "E690", {"start": v(17.6, -116.64) * mm, "mid": v(17.78, -116.28) * mm, "end": v(18.15, -116.1) * mm});
            skLineSegment(sketch, "E691", {"start": v(17.6, -116.64) * mm, "end": v(17.18, -118.93) * mm});
            skLineSegment(sketch, "E692", {"start": v(17.18, -118.93) * mm, "end": v(16.73, -120.85) * mm});
            skArc(sketch, "E693", {"start": v(16.73, -120.85) * mm, "mid": v(15.92, -120.96) * mm, "end": v(15.12, -121.06) * mm});
            skLineSegment(sketch, "E694", {"start": v(13.19, -117.22) * mm, "end": v(14.18, -119.33) * mm});
            skLineSegment(sketch, "E695", {"start": v(14.18, -119.33) * mm, "end": v(15.12, -121.06) * mm});
            skArc(sketch, "E696", {"start": v(12.52, -116.83) * mm, "mid": v(12.92, -116.92) * mm, "end": v(13.19, -117.22) * mm});
            skArc(sketch, "E697", {"start": v(12.52, -116.83) * mm, "mid": v(12.28, -116.86) * mm, "end": v(12.05, -116.88) * mm});
            skArc(sketch, "E698", {"start": v(11.47, -117.4) * mm, "mid": v(11.67, -117.05) * mm, "end": v(12.05, -116.88) * mm});
            skLineSegment(sketch, "E699", {"start": v(11.47, -117.4) * mm, "end": v(10.94, -119.67) * mm});
            skLineSegment(sketch, "E700", {"start": v(10.94, -119.67) * mm, "end": v(10.38, -121.56) * mm});
            skArc(sketch, "E701", {"start": v(10.38, -121.56) * mm, "mid": v(9.57, -121.62) * mm, "end": v(8.76, -121.68) * mm});
            skLineSegment(sketch, "E702", {"start": v(7.04, -117.75) * mm, "end": v(7.92, -119.9) * mm});
            skLineSegment(sketch, "E703", {"start": v(7.92, -119.9) * mm, "end": v(8.76, -121.68) * mm});
            skArc(sketch, "E704", {"start": v(6.39, -117.33) * mm, "mid": v(6.78, -117.43) * mm, "end": v(7.04, -117.75) * mm});
            skArc(sketch, "E705", {"start": v(6.39, -117.33) * mm, "mid": v(6.15, -117.34) * mm, "end": v(5.91, -117.35) * mm});
            skArc(sketch, "E706", {"start": v(5.3, -117.84) * mm, "mid": v(5.53, -117.5) * mm, "end": v(5.91, -117.35) * mm});
            skLineSegment(sketch, "E707", {"start": v(5.3, -117.84) * mm, "end": v(4.66, -120.08) * mm});
            skLineSegment(sketch, "E708", {"start": v(4.66, -120.08) * mm, "end": v(4, -121.93) * mm});
            skArc(sketch, "E709", {"start": v(4, -121.93) * mm, "mid": v(3.2, -121.96) * mm, "end": v(2.38, -121.98) * mm});
            skLineSegment(sketch, "E710", {"start": v(0.86, -117.96) * mm, "end": v(1.63, -120.15) * mm});
            skLineSegment(sketch, "E711", {"start": v(1.63, -120.15) * mm, "end": v(2.38, -121.98) * mm});
            skArc(sketch, "E712", {"start": v(0.24, -117.5) * mm, "mid": v(0.63, -117.63) * mm, "end": v(0.86, -117.96) * mm});
            skArc(sketch, "E713", {"start": v(0.24, -117.5) * mm, "mid": v(0, -117.5) * mm, "end": v(-0.24, -117.5) * mm});
            skArc(sketch, "E714", {"start": v(-0.86, -117.96) * mm, "mid": v(-0.63, -117.63) * mm, "end": v(-0.24, -117.5) * mm});
            skLineSegment(sketch, "E715", {"start": v(-0.86, -117.96) * mm, "end": v(-1.63, -120.15) * mm});
            skLineSegment(sketch, "E716", {"start": v(-1.63, -120.15) * mm, "end": v(-2.38, -121.98) * mm});
            skArc(sketch, "E717", {"start": v(-2.38, -121.98) * mm, "mid": v(-3.2, -121.96) * mm, "end": v(-4, -121.93) * mm});
            skLineSegment(sketch, "E718", {"start": v(-5.3, -117.84) * mm, "end": v(-4.66, -120.08) * mm});
            skLineSegment(sketch, "E719", {"start": v(-4.66, -120.08) * mm, "end": v(-4, -121.93) * mm});
            skArc(sketch, "E720", {"start": v(-5.91, -117.35) * mm, "mid": v(-5.53, -117.5) * mm, "end": v(-5.3, -117.84) * mm});
            skArc(sketch, "E721", {"start": v(-5.91, -117.35) * mm, "mid": v(-6.15, -117.34) * mm, "end": v(-6.39, -117.33) * mm});
            skArc(sketch, "E722", {"start": v(-7.04, -117.75) * mm, "mid": v(-6.78, -117.43) * mm, "end": v(-6.39, -117.33) * mm});
            skLineSegment(sketch, "E723", {"start": v(-7.04, -117.75) * mm, "end": v(-7.92, -119.9) * mm});
            skLineSegment(sketch, "E724", {"start": v(-7.92, -119.9) * mm, "end": v(-8.76, -121.68) * mm});
            skArc(sketch, "E725", {"start": v(-8.76, -121.68) * mm, "mid": v(-9.57, -121.62) * mm, "end": v(-10.38, -121.56) * mm});
            skLineSegment(sketch, "E726", {"start": v(-11.47, -117.4) * mm, "end": v(-10.94, -119.67) * mm});
            skLineSegment(sketch, "E727", {"start": v(-10.94, -119.67) * mm, "end": v(-10.38, -121.56) * mm});
            skArc(sketch, "E728", {"start": v(-12.05, -116.88) * mm, "mid": v(-11.67, -117.05) * mm, "end": v(-11.47, -117.4) * mm});
            skArc(sketch, "E729", {"start": v(-12.05, -116.88) * mm, "mid": v(-12.28, -116.86) * mm, "end": v(-12.52, -116.83) * mm});
            skArc(sketch, "E730", {"start": v(-13.19, -117.22) * mm, "mid": v(-12.92, -116.92) * mm, "end": v(-12.52, -116.83) * mm});
            skLineSegment(sketch, "E731", {"start": v(-13.19, -117.22) * mm, "end": v(-14.18, -119.33) * mm});
            skLineSegment(sketch, "E732", {"start": v(-14.18, -119.33) * mm, "end": v(-15.12, -121.06) * mm});
            skArc(sketch, "E733", {"start": v(-15.12, -121.06) * mm, "mid": v(-15.92, -120.96) * mm, "end": v(-16.73, -120.85) * mm});
            skLineSegment(sketch, "E734", {"start": v(-17.6, -116.64) * mm, "end": v(-17.18, -118.93) * mm});
            skLineSegment(sketch, "E735", {"start": v(-17.18, -118.93) * mm, "end": v(-16.73, -120.85) * mm});
            skArc(sketch, "E736", {"start": v(-18.15, -116.1) * mm, "mid": v(-17.78, -116.28) * mm, "end": v(-17.6, -116.64) * mm});
            skArc(sketch, "E737", {"start": v(-18.15, -116.1) * mm, "mid": v(-18.38, -116.05) * mm, "end": v(-18.62, -116.02) * mm});
            skArc(sketch, "E738", {"start": v(-19.3, -116.37) * mm, "mid": v(-19.02, -116.08) * mm, "end": v(-18.62, -116.02) * mm});
            skLineSegment(sketch, "E739", {"start": v(-19.3, -116.37) * mm, "end": v(-20.4, -118.42) * mm});
            skLineSegment(sketch, "E740", {"start": v(-20.4, -118.42) * mm, "end": v(-21.44, -120.1) * mm});
            skArc(sketch, "E741", {"start": v(-21.44, -120.1) * mm, "mid": v(-22.23, -119.96) * mm, "end": v(-23.03, -119.8) * mm});
            skLineSegment(sketch, "E742", {"start": v(-23.68, -115.56) * mm, "end": v(-23.38, -117.87) * mm});
            skLineSegment(sketch, "E743", {"start": v(-23.38, -117.87) * mm, "end": v(-23.03, -119.8) * mm});
            skArc(sketch, "E744", {"start": v(-24.2, -114.98) * mm, "mid": v(-23.84, -115.19) * mm, "end": v(-23.68, -115.56) * mm});
            skArc(sketch, "E745", {"start": v(-24.2, -114.98) * mm, "mid": v(-24.43, -114.93) * mm, "end": v(-24.66, -114.88) * mm});
            skArc(sketch, "E746", {"start": v(-25.37, -115.2) * mm, "mid": v(-25.07, -114.93) * mm, "end": v(-24.66, -114.88) * mm});
            skLineSegment(sketch, "E747", {"start": v(-25.37, -115.2) * mm, "end": v(-26.58, -117.19) * mm});
            skLineSegment(sketch, "E748", {"start": v(-26.58, -117.19) * mm, "end": v(-27.7, -118.82) * mm});
            skArc(sketch, "E749", {"start": v(-27.7, -118.82) * mm, "mid": v(-28.48, -118.63) * mm, "end": v(-29.27, -118.44) * mm});
            skLineSegment(sketch, "E750", {"start": v(-29.7, -114.16) * mm, "end": v(-29.52, -116.48) * mm});
            skLineSegment(sketch, "E751", {"start": v(-29.52, -116.48) * mm, "end": v(-29.27, -118.44) * mm});
            skArc(sketch, "E752", {"start": v(-30.18, -113.56) * mm, "mid": v(-29.84, -113.78) * mm, "end": v(-29.7, -114.16) * mm});
            skArc(sketch, "E753", {"start": v(-30.18, -113.56) * mm, "mid": v(-30.41, -113.5) * mm, "end": v(-30.64, -113.43) * mm});
            skArc(sketch, "E754", {"start": v(-31.36, -113.71) * mm, "mid": v(-31.05, -113.46) * mm, "end": v(-30.64, -113.43) * mm});
            skLineSegment(sketch, "E755", {"start": v(-31.36, -113.71) * mm, "end": v(-32.68, -115.64) * mm});
            skLineSegment(sketch, "E756", {"start": v(-32.68, -115.64) * mm, "end": v(-33.87, -117.2) * mm});
            skArc(sketch, "E757", {"start": v(-33.87, -117.2) * mm, "mid": v(-34.65, -116.98) * mm, "end": v(-35.43, -116.74) * mm});
            skLineSegment(sketch, "E758", {"start": v(-35.63, -112.45) * mm, "end": v(-35.58, -114.78) * mm});
            skLineSegment(sketch, "E759", {"start": v(-35.58, -114.78) * mm, "end": v(-35.43, -116.74) * mm});
            skArc(sketch, "E760", {"start": v(-36.08, -111.82) * mm, "mid": v(-35.75, -112.06) * mm, "end": v(-35.63, -112.45) * mm});
            skArc(sketch, "E761", {"start": v(-36.08, -111.82) * mm, "mid": v(-36.3, -111.75) * mm, "end": v(-36.54, -111.68) * mm});
            skArc(sketch, "E762", {"start": v(-37.27, -111.92) * mm, "mid": v(-36.94, -111.68) * mm, "end": v(-36.54, -111.68) * mm});
            skLineSegment(sketch, "E763", {"start": v(-37.27, -111.92) * mm, "end": v(-38.68, -113.77) * mm});
            skLineSegment(sketch, "E764", {"start": v(-38.68, -113.77) * mm, "end": v(-39.96, -115.27) * mm});
            skArc(sketch, "E765", {"start": v(-39.96, -115.27) * mm, "mid": v(-40.72, -115) * mm, "end": v(-41.49, -114.73) * mm});
            skLineSegment(sketch, "E766", {"start": v(-41.47, -110.43) * mm, "end": v(-41.54, -112.76) * mm});
            skLineSegment(sketch, "E767", {"start": v(-41.54, -112.76) * mm, "end": v(-41.49, -114.73) * mm});
            skArc(sketch, "E768", {"start": v(-41.89, -109.78) * mm, "mid": v(-41.57, -110.04) * mm, "end": v(-41.47, -110.43) * mm});
            skArc(sketch, "E769", {"start": v(-41.89, -109.78) * mm, "mid": v(-42.1, -109.7) * mm, "end": v(-42.33, -109.61) * mm});
            skArc(sketch, "E770", {"start": v(-43.08, -109.81) * mm, "mid": v(-42.74, -109.59) * mm, "end": v(-42.33, -109.61) * mm});
            skLineSegment(sketch, "E771", {"start": v(-43.08, -109.81) * mm, "end": v(-44.58, -111.59) * mm});
            skLineSegment(sketch, "E772", {"start": v(-44.58, -111.59) * mm, "end": v(-45.94, -113.02) * mm});
            skArc(sketch, "E773", {"start": v(-45.94, -113.02) * mm, "mid": v(-46.69, -112.71) * mm, "end": v(-47.43, -112.4) * mm});
            skLineSegment(sketch, "E774", {"start": v(-47.19, -108.11) * mm, "end": v(-47.38, -110.43) * mm});
            skLineSegment(sketch, "E775", {"start": v(-47.38, -110.43) * mm, "end": v(-47.43, -112.4) * mm});
            skArc(sketch, "E776", {"start": v(-47.57, -107.44) * mm, "mid": v(-47.27, -107.71) * mm, "end": v(-47.19, -108.11) * mm});
            skArc(sketch, "E777", {"start": v(-47.57, -107.44) * mm, "mid": v(-47.8, -107.34) * mm, "end": v(-48, -107.24) * mm});
            skArc(sketch, "E778", {"start": v(-48.77, -107.4) * mm, "mid": v(-48.42, -107.2) * mm, "end": v(-48, -107.24) * mm});
            skLineSegment(sketch, "E779", {"start": v(-48.77, -107.4) * mm, "end": v(-50.36, -109.1) * mm});
            skLineSegment(sketch, "E780", {"start": v(-50.36, -109.1) * mm, "end": v(-51.8, -110.46) * mm});
            skArc(sketch, "E781", {"start": v(-51.8, -110.46) * mm, "mid": v(-52.52, -110.12) * mm, "end": v(-53.25, -109.76) * mm});
            skLineSegment(sketch, "E782", {"start": v(-52.78, -105.5) * mm, "end": v(-53.1, -107.8) * mm});
            skLineSegment(sketch, "E783", {"start": v(-53.1, -107.8) * mm, "end": v(-53.25, -109.76) * mm});
            skArc(sketch, "E784", {"start": v(-53.13, -104.8) * mm, "mid": v(-52.84, -105.1) * mm, "end": v(-52.78, -105.5) * mm});
            skArc(sketch, "E785", {"start": v(-53.13, -104.8) * mm, "mid": v(-53.34, -104.7) * mm, "end": v(-53.56, -104.58) * mm});
            skArc(sketch, "E786", {"start": v(-54.32, -104.7) * mm, "mid": v(-53.96, -104.52) * mm, "end": v(-53.56, -104.58) * mm});
            skLineSegment(sketch, "E787", {"start": v(-54.32, -104.7) * mm, "end": v(-56, -106.32) * mm});
            skLineSegment(sketch, "E788", {"start": v(-56, -106.32) * mm, "end": v(-57.5, -107.6) * mm});
            skArc(sketch, "E789", {"start": v(-57.5, -107.6) * mm, "mid": v(-58.21, -107.22) * mm, "end": v(-58.92, -106.83) * mm});
            skLineSegment(sketch, "E790", {"start": v(-58.23, -102.59) * mm, "end": v(-58.66, -104.87) * mm});
            skLineSegment(sketch, "E791", {"start": v(-58.66, -104.87) * mm, "end": v(-58.92, -106.83) * mm});
            skArc(sketch, "E792", {"start": v(-58.54, -101.88) * mm, "mid": v(-58.27, -102.18) * mm, "end": v(-58.23, -102.59) * mm});
            skArc(sketch, "E793", {"start": v(-58.54, -101.88) * mm, "mid": v(-58.75, -101.76) * mm, "end": v(-58.96, -101.64) * mm});
            skArc(sketch, "E794", {"start": v(-59.73, -101.72) * mm, "mid": v(-59.36, -101.55) * mm, "end": v(-58.96, -101.64) * mm});
            skLineSegment(sketch, "E795", {"start": v(-59.73, -101.72) * mm, "end": v(-61.5, -103.24) * mm});
            skLineSegment(sketch, "E796", {"start": v(-61.5, -103.24) * mm, "end": v(-63.05, -104.44) * mm});
            skArc(sketch, "E797", {"start": v(-63.05, -104.44) * mm, "mid": v(-63.74, -104.02) * mm, "end": v(-64.43, -103.6) * mm});
            skLineSegment(sketch, "E798", {"start": v(-63.52, -99.4) * mm, "end": v(-64.07, -101.66) * mm});
            skLineSegment(sketch, "E799", {"start": v(-64.07, -101.66) * mm, "end": v(-64.43, -103.6) * mm});
            skArc(sketch, "E800", {"start": v(-63.8, -98.67) * mm, "mid": v(-63.54, -99) * mm, "end": v(-63.52, -99.4) * mm});
            skArc(sketch, "E801", {"start": v(-63.8, -98.67) * mm, "mid": v(-64, -98.54) * mm, "end": v(-64.2, -98.41) * mm});
            skArc(sketch, "E802", {"start": v(-64.97, -98.46) * mm, "mid": v(-64.59, -98.3) * mm, "end": v(-64.2, -98.41) * mm});
            skLineSegment(sketch, "E803", {"start": v(-64.97, -98.46) * mm, "end": v(-66.8, -99.88) * mm});
            skLineSegment(sketch, "E804", {"start": v(-66.8, -99.88) * mm, "end": v(-68.43, -101) * mm});
            skArc(sketch, "E805", {"start": v(-68.43, -101) * mm, "mid": v(-69.1, -100.54) * mm, "end": v(-69.77, -100.08) * mm});
            skLineSegment(sketch, "E806", {"start": v(-68.63, -95.94) * mm, "end": v(-69.3, -98.17) * mm});
            skLineSegment(sketch, "E807", {"start": v(-69.3, -98.17) * mm, "end": v(-69.77, -100.08) * mm});
            skArc(sketch, "E808", {"start": v(-68.87, -95.2) * mm, "mid": v(-68.63, -95.53) * mm, "end": v(-68.63, -95.94) * mm});
            skArc(sketch, "E809", {"start": v(-68.87, -95.2) * mm, "mid": v(-69.06, -95.06) * mm, "end": v(-69.26, -94.92) * mm});
            skArc(sketch, "E810", {"start": v(-70.03, -94.92) * mm, "mid": v(-69.65, -94.8) * mm, "end": v(-69.26, -94.92) * mm});
            skLineSegment(sketch, "E811", {"start": v(-70.03, -94.92) * mm, "end": v(-71.95, -96.25) * mm});
            skLineSegment(sketch, "E812", {"start": v(-71.95, -96.25) * mm, "end": v(-73.62, -97.28) * mm});
            skArc(sketch, "E813", {"start": v(-73.62, -97.28) * mm, "mid": v(-74.27, -96.79) * mm, "end": v(-74.9, -96.3) * mm});
            skLineSegment(sketch, "E814", {"start": v(-73.56, -92.21) * mm, "end": v(-74.35, -94.4) * mm});
            skLineSegment(sketch, "E815", {"start": v(-74.35, -94.4) * mm, "end": v(-74.9, -96.3) * mm});
            skArc(sketch, "E816", {"start": v(-73.76, -91.46) * mm, "mid": v(-73.54, -91.8) * mm, "end": v(-73.56, -92.21) * mm});
            skArc(sketch, "E817", {"start": v(-73.76, -91.46) * mm, "mid": v(-73.95, -91.31) * mm, "end": v(-74.13, -91.16) * mm});
            skArc(sketch, "E818", {"start": v(-74.9, -91.13) * mm, "mid": v(-74.51, -91.02) * mm, "end": v(-74.13, -91.16) * mm});
            skLineSegment(sketch, "E819", {"start": v(-74.9, -91.13) * mm, "end": v(-76.88, -92.35) * mm});
            skLineSegment(sketch, "E820", {"start": v(-76.88, -92.35) * mm, "end": v(-78.62, -93.3) * mm});
            skArc(sketch, "E821", {"start": v(-78.62, -93.3) * mm, "mid": v(-79.23, -92.77) * mm, "end": v(-79.85, -92.24) * mm});
            skLineSegment(sketch, "E822", {"start": v(-78.29, -88.24) * mm, "end": v(-79.19, -90.38) * mm});
            skLineSegment(sketch, "E823", {"start": v(-79.19, -90.38) * mm, "end": v(-79.85, -92.24) * mm});
            skArc(sketch, "E824", {"start": v(-78.45, -87.48) * mm, "mid": v(-78.24, -87.83) * mm, "end": v(-78.29, -88.24) * mm});
            skArc(sketch, "E825", {"start": v(-78.45, -87.48) * mm, "mid": v(-78.62, -87.32) * mm, "end": v(-78.8, -87.16) * mm});
            skArc(sketch, "E826", {"start": v(-79.57, -87.08) * mm, "mid": v(-79.17, -87) * mm, "end": v(-78.8, -87.16) * mm});
            skLineSegment(sketch, "E827", {"start": v(-79.57, -87.08) * mm, "end": v(-81.61, -88.2) * mm});
            skLineSegment(sketch, "E828", {"start": v(-81.61, -88.2) * mm, "end": v(-83.4, -89.05) * mm});
            skArc(sketch, "E829", {"start": v(-83.4, -89.05) * mm, "mid": v(-83.98, -88.5) * mm, "end": v(-84.56, -87.94) * mm});
            skLineSegment(sketch, "E830", {"start": v(-82.8, -84.02) * mm, "end": v(-83.8, -86.12) * mm});
            skLineSegment(sketch, "E831", {"start": v(-83.8, -86.12) * mm, "end": v(-84.56, -87.94) * mm});
            skArc(sketch, "E832", {"start": v(-82.92, -83.25) * mm, "mid": v(-82.73, -83.62) * mm, "end": v(-82.8, -84.02) * mm});
            skArc(sketch, "E833", {"start": v(-82.92, -83.25) * mm, "mid": v(-83.09, -83.09) * mm, "end": v(-83.25, -82.92) * mm});
            skArc(sketch, "E834", {"start": v(-84.02, -82.8) * mm, "mid": v(-83.62, -82.73) * mm, "end": v(-83.25, -82.92) * mm});
            skLineSegment(sketch, "E835", {"start": v(-84.02, -82.8) * mm, "end": v(-86.12, -83.8) * mm});
            skLineSegment(sketch, "E836", {"start": v(-86.12, -83.8) * mm, "end": v(-87.94, -84.56) * mm});
            skArc(sketch, "E837", {"start": v(-87.94, -84.56) * mm, "mid": v(-88.5, -83.98) * mm, "end": v(-89.05, -83.4) * mm});
            skLineSegment(sketch, "E838", {"start": v(-87.08, -79.57) * mm, "end": v(-88.2, -81.61) * mm});
            skLineSegment(sketch, "E839", {"start": v(-88.2, -81.61) * mm, "end": v(-89.05, -83.4) * mm});
            skArc(sketch, "E840", {"start": v(-87.16, -78.8) * mm, "mid": v(-87, -79.17) * mm, "end": v(-87.08, -79.57) * mm});
            skArc(sketch, "E841", {"start": v(-87.16, -78.8) * mm, "mid": v(-87.32, -78.62) * mm, "end": v(-87.48, -78.45) * mm});
            skArc(sketch, "E842", {"start": v(-88.24, -78.29) * mm, "mid": v(-87.83, -78.24) * mm, "end": v(-87.48, -78.45) * mm});
            skLineSegment(sketch, "E843", {"start": v(-88.24, -78.29) * mm, "end": v(-90.38, -79.19) * mm});
            skLineSegment(sketch, "E844", {"start": v(-90.38, -79.19) * mm, "end": v(-92.24, -79.85) * mm});
            skArc(sketch, "E845", {"start": v(-92.24, -79.85) * mm, "mid": v(-92.77, -79.23) * mm, "end": v(-93.3, -78.62) * mm});
            skLineSegment(sketch, "E846", {"start": v(-91.13, -74.9) * mm, "end": v(-92.35, -76.88) * mm});
            skLineSegment(sketch, "E847", {"start": v(-92.35, -76.88) * mm, "end": v(-93.3, -78.62) * mm});
            skArc(sketch, "E848", {"start": v(-91.16, -74.13) * mm, "mid": v(-91.02, -74.51) * mm, "end": v(-91.13, -74.9) * mm});
            skArc(sketch, "E849", {"start": v(-91.16, -74.13) * mm, "mid": v(-91.31, -73.95) * mm, "end": v(-91.46, -73.76) * mm});
            skArc(sketch, "E850", {"start": v(-92.21, -73.56) * mm, "mid": v(-91.8, -73.54) * mm, "end": v(-91.46, -73.76) * mm});
            skLineSegment(sketch, "E851", {"start": v(-92.21, -73.56) * mm, "end": v(-94.4, -74.35) * mm});
            skLineSegment(sketch, "E852", {"start": v(-94.4, -74.35) * mm, "end": v(-96.3, -74.9) * mm});
            skArc(sketch, "E853", {"start": v(-96.3, -74.9) * mm, "mid": v(-96.79, -74.27) * mm, "end": v(-97.28, -73.62) * mm});
            skLineSegment(sketch, "E854", {"start": v(-94.92, -70.03) * mm, "end": v(-96.25, -71.95) * mm});
            skLineSegment(sketch, "E855", {"start": v(-96.25, -71.95) * mm, "end": v(-97.28, -73.62) * mm});
            skArc(sketch, "E856", {"start": v(-94.92, -69.26) * mm, "mid": v(-94.8, -69.65) * mm, "end": v(-94.92, -70.03) * mm});
            skArc(sketch, "E857", {"start": v(-94.92, -69.26) * mm, "mid": v(-95.06, -69.06) * mm, "end": v(-95.2, -68.87) * mm});
            skArc(sketch, "E858", {"start": v(-95.94, -68.63) * mm, "mid": v(-95.53, -68.63) * mm, "end": v(-95.2, -68.87) * mm});
            skLineSegment(sketch, "E859", {"start": v(-95.94, -68.63) * mm, "end": v(-98.17, -69.3) * mm});
            skLineSegment(sketch, "E860", {"start": v(-98.17, -69.3) * mm, "end": v(-100.08, -69.77) * mm});
            skArc(sketch, "E861", {"start": v(-100.08, -69.77) * mm, "mid": v(-100.54, -69.1) * mm, "end": v(-101, -68.43) * mm});
            skLineSegment(sketch, "E862", {"start": v(-98.46, -64.97) * mm, "end": v(-99.88, -66.8) * mm});
            skLineSegment(sketch, "E863", {"start": v(-99.88, -66.8) * mm, "end": v(-101, -68.43) * mm});
            skArc(sketch, "E864", {"start": v(-98.41, -64.2) * mm, "mid": v(-98.3, -64.59) * mm, "end": v(-98.46, -64.97) * mm});
            skArc(sketch, "E865", {"start": v(-98.41, -64.2) * mm, "mid": v(-98.54, -64) * mm, "end": v(-98.67, -63.8) * mm});
            skArc(sketch, "E866", {"start": v(-99.4, -63.52) * mm, "mid": v(-99, -63.54) * mm, "end": v(-98.67, -63.8) * mm});
            skLineSegment(sketch, "E867", {"start": v(-99.4, -63.52) * mm, "end": v(-101.66, -64.07) * mm});
            skLineSegment(sketch, "E868", {"start": v(-101.66, -64.07) * mm, "end": v(-103.6, -64.43) * mm});
            skArc(sketch, "E869", {"start": v(-103.6, -64.43) * mm, "mid": v(-104.02, -63.74) * mm, "end": v(-104.44, -63.05) * mm});
            skLineSegment(sketch, "E870", {"start": v(-101.72, -59.73) * mm, "end": v(-103.24, -61.5) * mm});
            skLineSegment(sketch, "E871", {"start": v(-103.24, -61.5) * mm, "end": v(-104.44, -63.05) * mm});
            skArc(sketch, "E872", {"start": v(-101.64, -58.96) * mm, "mid": v(-101.55, -59.36) * mm, "end": v(-101.72, -59.73) * mm});
            skArc(sketch, "E873", {"start": v(-101.64, -58.96) * mm, "mid": v(-101.76, -58.75) * mm, "end": v(-101.88, -58.54) * mm});
            skArc(sketch, "E874", {"start": v(-102.59, -58.23) * mm, "mid": v(-102.18, -58.27) * mm, "end": v(-101.88, -58.54) * mm});
            skLineSegment(sketch, "E875", {"start": v(-102.59, -58.23) * mm, "end": v(-104.87, -58.66) * mm});
            skLineSegment(sketch, "E876", {"start": v(-104.87, -58.66) * mm, "end": v(-106.83, -58.92) * mm});
            skArc(sketch, "E877", {"start": v(-106.83, -58.92) * mm, "mid": v(-107.22, -58.21) * mm, "end": v(-107.6, -57.5) * mm});
            skLineSegment(sketch, "E878", {"start": v(-104.7, -54.32) * mm, "end": v(-106.32, -56) * mm});
            skLineSegment(sketch, "E879", {"start": v(-106.32, -56) * mm, "end": v(-107.6, -57.5) * mm});
            skArc(sketch, "E880", {"start": v(-104.58, -53.56) * mm, "mid": v(-104.52, -53.96) * mm, "end": v(-104.7, -54.32) * mm});
            skArc(sketch, "E881", {"start": v(-104.58, -53.56) * mm, "mid": v(-104.7, -53.34) * mm, "end": v(-104.8, -53.13) * mm});
            skArc(sketch, "E882", {"start": v(-105.5, -52.78) * mm, "mid": v(-105.1, -52.84) * mm, "end": v(-104.8, -53.13) * mm});
            skLineSegment(sketch, "E883", {"start": v(-105.5, -52.78) * mm, "end": v(-107.8, -53.1) * mm});
            skLineSegment(sketch, "E884", {"start": v(-107.8, -53.1) * mm, "end": v(-109.76, -53.25) * mm});
            skArc(sketch, "E885", {"start": v(-109.76, -53.25) * mm, "mid": v(-110.12, -52.52) * mm, "end": v(-110.46, -51.8) * mm});
            skLineSegment(sketch, "E886", {"start": v(-107.4, -48.77) * mm, "end": v(-109.1, -50.36) * mm});
            skLineSegment(sketch, "E887", {"start": v(-109.1, -50.36) * mm, "end": v(-110.46, -51.8) * mm});
            skArc(sketch, "E888", {"start": v(-107.24, -48) * mm, "mid": v(-107.2, -48.42) * mm, "end": v(-107.4, -48.77) * mm});
            skArc(sketch, "E889", {"start": v(-107.24, -48) * mm, "mid": v(-107.34, -47.8) * mm, "end": v(-107.44, -47.57) * mm});
            skArc(sketch, "E890", {"start": v(-108.11, -47.19) * mm, "mid": v(-107.71, -47.27) * mm, "end": v(-107.44, -47.57) * mm});
            skLineSegment(sketch, "E891", {"start": v(-108.11, -47.19) * mm, "end": v(-110.43, -47.38) * mm});
            skLineSegment(sketch, "E892", {"start": v(-110.43, -47.38) * mm, "end": v(-112.4, -47.43) * mm});
            skArc(sketch, "E893", {"start": v(-112.4, -47.43) * mm, "mid": v(-112.71, -46.69) * mm, "end": v(-113.02, -45.94) * mm});
            skLineSegment(sketch, "E894", {"start": v(-109.81, -43.08) * mm, "end": v(-111.59, -44.58) * mm});
            skLineSegment(sketch, "E895", {"start": v(-111.59, -44.58) * mm, "end": v(-113.02, -45.94) * mm});
            skArc(sketch, "E896", {"start": v(-109.61, -42.33) * mm, "mid": v(-109.59, -42.74) * mm, "end": v(-109.81, -43.08) * mm});
            skArc(sketch, "E897", {"start": v(-109.61, -42.33) * mm, "mid": v(-109.7, -42.1) * mm, "end": v(-109.78, -41.89) * mm});
            skArc(sketch, "E898", {"start": v(-110.43, -41.47) * mm, "mid": v(-110.04, -41.57) * mm, "end": v(-109.78, -41.89) * mm});
            skLineSegment(sketch, "E899", {"start": v(-110.43, -41.47) * mm, "end": v(-112.76, -41.54) * mm});
            skLineSegment(sketch, "E900", {"start": v(-112.76, -41.54) * mm, "end": v(-114.73, -41.49) * mm});
            skArc(sketch, "E901", {"start": v(-114.73, -41.49) * mm, "mid": v(-115, -40.72) * mm, "end": v(-115.27, -39.96) * mm});
            skLineSegment(sketch, "E902", {"start": v(-111.92, -37.27) * mm, "end": v(-113.77, -38.68) * mm});
            skLineSegment(sketch, "E903", {"start": v(-113.77, -38.68) * mm, "end": v(-115.27, -39.96) * mm});
            skArc(sketch, "E904", {"start": v(-111.68, -36.54) * mm, "mid": v(-111.68, -36.94) * mm, "end": v(-111.92, -37.27) * mm});
            skArc(sketch, "E905", {"start": v(-111.68, -36.54) * mm, "mid": v(-111.75, -36.3) * mm, "end": v(-111.82, -36.08) * mm});
            skArc(sketch, "E906", {"start": v(-112.45, -35.63) * mm, "mid": v(-112.06, -35.75) * mm, "end": v(-111.82, -36.08) * mm});
            skLineSegment(sketch, "E907", {"start": v(-112.45, -35.63) * mm, "end": v(-114.78, -35.58) * mm});
            skLineSegment(sketch, "E908", {"start": v(-114.78, -35.58) * mm, "end": v(-116.74, -35.43) * mm});
            skArc(sketch, "E909", {"start": v(-116.74, -35.43) * mm, "mid": v(-116.98, -34.65) * mm, "end": v(-117.2, -33.87) * mm});
            skLineSegment(sketch, "E910", {"start": v(-113.71, -31.36) * mm, "end": v(-115.64, -32.68) * mm});
            skLineSegment(sketch, "E911", {"start": v(-115.64, -32.68) * mm, "end": v(-117.2, -33.87) * mm});
            skArc(sketch, "E912", {"start": v(-113.43, -30.64) * mm, "mid": v(-113.46, -31.05) * mm, "end": v(-113.71, -31.36) * mm});
            skArc(sketch, "E913", {"start": v(-113.43, -30.64) * mm, "mid": v(-113.5, -30.41) * mm, "end": v(-113.56, -30.18) * mm});
            skArc(sketch, "E914", {"start": v(-114.16, -29.7) * mm, "mid": v(-113.78, -29.84) * mm, "end": v(-113.56, -30.18) * mm});
            skLineSegment(sketch, "E915", {"start": v(-114.16, -29.7) * mm, "end": v(-116.48, -29.52) * mm});
            skLineSegment(sketch, "E916", {"start": v(-116.48, -29.52) * mm, "end": v(-118.44, -29.27) * mm});
            skArc(sketch, "E917", {"start": v(-118.44, -29.27) * mm, "mid": v(-118.63, -28.48) * mm, "end": v(-118.82, -27.7) * mm});
            skLineSegment(sketch, "E918", {"start": v(-115.2, -25.37) * mm, "end": v(-117.19, -26.58) * mm});
            skLineSegment(sketch, "E919", {"start": v(-117.19, -26.58) * mm, "end": v(-118.82, -27.7) * mm});
            skArc(sketch, "E920", {"start": v(-114.88, -24.66) * mm, "mid": v(-114.93, -25.07) * mm, "end": v(-115.2, -25.37) * mm});
            skArc(sketch, "E921", {"start": v(-114.88, -24.66) * mm, "mid": v(-114.93, -24.43) * mm, "end": v(-114.98, -24.2) * mm});
            skArc(sketch, "E922", {"start": v(-115.56, -23.68) * mm, "mid": v(-115.19, -23.84) * mm, "end": v(-114.98, -24.2) * mm});
            skLineSegment(sketch, "E923", {"start": v(-115.56, -23.68) * mm, "end": v(-117.87, -23.38) * mm});
            skLineSegment(sketch, "E924", {"start": v(-117.87, -23.38) * mm, "end": v(-119.8, -23.03) * mm});
            skArc(sketch, "E925", {"start": v(-119.8, -23.03) * mm, "mid": v(-119.96, -22.23) * mm, "end": v(-120.1, -21.44) * mm});
            skLineSegment(sketch, "E926", {"start": v(-116.37, -19.3) * mm, "end": v(-118.42, -20.4) * mm});
            skLineSegment(sketch, "E927", {"start": v(-118.42, -20.4) * mm, "end": v(-120.1, -21.44) * mm});
            skArc(sketch, "E928", {"start": v(-116.02, -18.62) * mm, "mid": v(-116.08, -19.02) * mm, "end": v(-116.37, -19.3) * mm});
            skArc(sketch, "E929", {"start": v(-116.02, -18.62) * mm, "mid": v(-116.05, -18.38) * mm, "end": v(-116.1, -18.15) * mm});
            skArc(sketch, "E930", {"start": v(-116.64, -17.6) * mm, "mid": v(-116.28, -17.78) * mm, "end": v(-116.1, -18.15) * mm});
            skLineSegment(sketch, "E931", {"start": v(-116.64, -17.6) * mm, "end": v(-118.93, -17.18) * mm});
            skLineSegment(sketch, "E932", {"start": v(-118.93, -17.18) * mm, "end": v(-120.85, -16.73) * mm});
            skArc(sketch, "E933", {"start": v(-120.85, -16.73) * mm, "mid": v(-120.96, -15.92) * mm, "end": v(-121.06, -15.12) * mm});
            skLineSegment(sketch, "E934", {"start": v(-117.22, -13.19) * mm, "end": v(-119.33, -14.18) * mm});
            skLineSegment(sketch, "E935", {"start": v(-119.33, -14.18) * mm, "end": v(-121.06, -15.12) * mm});
            skArc(sketch, "E936", {"start": v(-116.83, -12.52) * mm, "mid": v(-116.92, -12.92) * mm, "end": v(-117.22, -13.19) * mm});
            skArc(sketch, "E937", {"start": v(-116.83, -12.52) * mm, "mid": v(-116.86, -12.28) * mm, "end": v(-116.88, -12.05) * mm});
            skArc(sketch, "E938", {"start": v(-117.4, -11.47) * mm, "mid": v(-117.05, -11.67) * mm, "end": v(-116.88, -12.05) * mm});
            skLineSegment(sketch, "E939", {"start": v(-117.4, -11.47) * mm, "end": v(-119.67, -10.94) * mm});
            skLineSegment(sketch, "E940", {"start": v(-119.67, -10.94) * mm, "end": v(-121.56, -10.38) * mm});
            skArc(sketch, "E941", {"start": v(-121.56, -10.38) * mm, "mid": v(-121.62, -9.57) * mm, "end": v(-121.68, -8.76) * mm});
            skLineSegment(sketch, "E942", {"start": v(-117.75, -7.04) * mm, "end": v(-119.9, -7.92) * mm});
            skLineSegment(sketch, "E943", {"start": v(-119.9, -7.92) * mm, "end": v(-121.68, -8.76) * mm});
            skArc(sketch, "E944", {"start": v(-117.33, -6.39) * mm, "mid": v(-117.43, -6.78) * mm, "end": v(-117.75, -7.04) * mm});
            skArc(sketch, "E945", {"start": v(-117.33, -6.39) * mm, "mid": v(-117.34, -6.15) * mm, "end": v(-117.35, -5.91) * mm});
            skArc(sketch, "E946", {"start": v(-117.84, -5.3) * mm, "mid": v(-117.5, -5.53) * mm, "end": v(-117.35, -5.91) * mm});
            skLineSegment(sketch, "E947", {"start": v(-117.84, -5.3) * mm, "end": v(-120.08, -4.66) * mm});
            skLineSegment(sketch, "E948", {"start": v(-120.08, -4.66) * mm, "end": v(-121.93, -4) * mm});
            skArc(sketch, "E949", {"start": v(-121.93, -4) * mm, "mid": v(-121.96, -3.2) * mm, "end": v(-121.98, -2.38) * mm});
            skLineSegment(sketch, "E950", {"start": v(-117.96, -0.86) * mm, "end": v(-120.15, -1.63) * mm});
            skLineSegment(sketch, "E951", {"start": v(-120.15, -1.63) * mm, "end": v(-121.98, -2.38) * mm});
            skArc(sketch, "E952", {"start": v(-117.5, -0.24) * mm, "mid": v(-117.63, -0.63) * mm, "end": v(-117.96, -0.86) * mm});
            skArc(sketch, "E953", {"start": v(-117.5, -0.24) * mm, "mid": v(-117.5, 0) * mm, "end": v(-117.5, 0.24) * mm});
            skArc(sketch, "E954", {"start": v(-117.96, 0.86) * mm, "mid": v(-117.63, 0.63) * mm, "end": v(-117.5, 0.24) * mm});
            skLineSegment(sketch, "E955", {"start": v(-117.96, 0.86) * mm, "end": v(-120.15, 1.63) * mm});
            skLineSegment(sketch, "E956", {"start": v(-120.15, 1.63) * mm, "end": v(-121.98, 2.38) * mm});
            skArc(sketch, "E957", {"start": v(-121.98, 2.38) * mm, "mid": v(-121.96, 3.2) * mm, "end": v(-121.93, 4) * mm});
            skLineSegment(sketch, "E958", {"start": v(-117.84, 5.3) * mm, "end": v(-120.08, 4.66) * mm});
            skLineSegment(sketch, "E959", {"start": v(-120.08, 4.66) * mm, "end": v(-121.93, 4) * mm});
            skArc(sketch, "E960", {"start": v(-117.35, 5.91) * mm, "mid": v(-117.5, 5.53) * mm, "end": v(-117.84, 5.3) * mm});
            skArc(sketch, "E961", {"start": v(-117.35, 5.91) * mm, "mid": v(-117.34, 6.15) * mm, "end": v(-117.33, 6.39) * mm});
            skArc(sketch, "E962", {"start": v(-117.75, 7.04) * mm, "mid": v(-117.43, 6.78) * mm, "end": v(-117.33, 6.39) * mm});
            skLineSegment(sketch, "E963", {"start": v(-117.75, 7.04) * mm, "end": v(-119.9, 7.92) * mm});
            skLineSegment(sketch, "E964", {"start": v(-119.9, 7.92) * mm, "end": v(-121.68, 8.76) * mm});
            skArc(sketch, "E965", {"start": v(-121.68, 8.76) * mm, "mid": v(-121.62, 9.57) * mm, "end": v(-121.56, 10.38) * mm});
            skLineSegment(sketch, "E966", {"start": v(-117.4, 11.47) * mm, "end": v(-119.67, 10.94) * mm});
            skLineSegment(sketch, "E967", {"start": v(-119.67, 10.94) * mm, "end": v(-121.56, 10.38) * mm});
            skArc(sketch, "E968", {"start": v(-116.88, 12.05) * mm, "mid": v(-117.05, 11.67) * mm, "end": v(-117.4, 11.47) * mm});
            skArc(sketch, "E969", {"start": v(-116.88, 12.05) * mm, "mid": v(-116.86, 12.28) * mm, "end": v(-116.83, 12.52) * mm});
            skArc(sketch, "E970", {"start": v(-117.22, 13.19) * mm, "mid": v(-116.92, 12.92) * mm, "end": v(-116.83, 12.52) * mm});
            skLineSegment(sketch, "E971", {"start": v(-117.22, 13.19) * mm, "end": v(-119.33, 14.18) * mm});
            skLineSegment(sketch, "E972", {"start": v(-119.33, 14.18) * mm, "end": v(-121.06, 15.12) * mm});
            skArc(sketch, "E973", {"start": v(-121.06, 15.12) * mm, "mid": v(-120.96, 15.92) * mm, "end": v(-120.85, 16.73) * mm});
            skLineSegment(sketch, "E974", {"start": v(-116.64, 17.6) * mm, "end": v(-118.93, 17.18) * mm});
            skLineSegment(sketch, "E975", {"start": v(-118.93, 17.18) * mm, "end": v(-120.85, 16.73) * mm});
            skArc(sketch, "E976", {"start": v(-116.1, 18.15) * mm, "mid": v(-116.28, 17.78) * mm, "end": v(-116.64, 17.6) * mm});
            skArc(sketch, "E977", {"start": v(-116.1, 18.15) * mm, "mid": v(-116.05, 18.38) * mm, "end": v(-116.02, 18.62) * mm});
            skArc(sketch, "E978", {"start": v(-116.37, 19.3) * mm, "mid": v(-116.08, 19.02) * mm, "end": v(-116.02, 18.62) * mm});
            skLineSegment(sketch, "E979", {"start": v(-116.37, 19.3) * mm, "end": v(-118.42, 20.4) * mm});
            skLineSegment(sketch, "E980", {"start": v(-118.42, 20.4) * mm, "end": v(-120.1, 21.44) * mm});
            skArc(sketch, "E981", {"start": v(-120.1, 21.44) * mm, "mid": v(-119.96, 22.23) * mm, "end": v(-119.8, 23.03) * mm});
            skLineSegment(sketch, "E982", {"start": v(-115.56, 23.68) * mm, "end": v(-117.87, 23.38) * mm});
            skLineSegment(sketch, "E983", {"start": v(-117.87, 23.38) * mm, "end": v(-119.8, 23.03) * mm});
            skArc(sketch, "E984", {"start": v(-114.98, 24.2) * mm, "mid": v(-115.19, 23.84) * mm, "end": v(-115.56, 23.68) * mm});
            skArc(sketch, "E985", {"start": v(-114.98, 24.2) * mm, "mid": v(-114.93, 24.43) * mm, "end": v(-114.88, 24.66) * mm});
            skArc(sketch, "E986", {"start": v(-115.2, 25.37) * mm, "mid": v(-114.93, 25.07) * mm, "end": v(-114.88, 24.66) * mm});
            skLineSegment(sketch, "E987", {"start": v(-115.2, 25.37) * mm, "end": v(-117.19, 26.58) * mm});
            skLineSegment(sketch, "E988", {"start": v(-117.19, 26.58) * mm, "end": v(-118.82, 27.7) * mm});
            skArc(sketch, "E989", {"start": v(-118.82, 27.7) * mm, "mid": v(-118.63, 28.48) * mm, "end": v(-118.44, 29.27) * mm});
            skLineSegment(sketch, "E990", {"start": v(-114.16, 29.7) * mm, "end": v(-116.48, 29.52) * mm});
            skLineSegment(sketch, "E991", {"start": v(-116.48, 29.52) * mm, "end": v(-118.44, 29.27) * mm});
            skArc(sketch, "E992", {"start": v(-113.56, 30.18) * mm, "mid": v(-113.78, 29.84) * mm, "end": v(-114.16, 29.7) * mm});
            skArc(sketch, "E993", {"start": v(-113.56, 30.18) * mm, "mid": v(-113.5, 30.41) * mm, "end": v(-113.43, 30.64) * mm});
            skArc(sketch, "E994", {"start": v(-113.71, 31.36) * mm, "mid": v(-113.46, 31.05) * mm, "end": v(-113.43, 30.64) * mm});
            skLineSegment(sketch, "E995", {"start": v(-113.71, 31.36) * mm, "end": v(-115.64, 32.68) * mm});
            skLineSegment(sketch, "E996", {"start": v(-115.64, 32.68) * mm, "end": v(-117.2, 33.87) * mm});
            skArc(sketch, "E997", {"start": v(-117.2, 33.87) * mm, "mid": v(-116.98, 34.65) * mm, "end": v(-116.74, 35.43) * mm});
            skLineSegment(sketch, "E998", {"start": v(-112.45, 35.63) * mm, "end": v(-114.78, 35.58) * mm});
            skLineSegment(sketch, "E999", {"start": v(-114.78, 35.58) * mm, "end": v(-116.74, 35.43) * mm});
            skArc(sketch, "E1000", {"start": v(-111.82, 36.08) * mm, "mid": v(-112.06, 35.75) * mm, "end": v(-112.45, 35.63) * mm});
            skArc(sketch, "E1001", {"start": v(-111.82, 36.08) * mm, "mid": v(-111.75, 36.3) * mm, "end": v(-111.68, 36.54) * mm});
            skArc(sketch, "E1002", {"start": v(-111.92, 37.27) * mm, "mid": v(-111.68, 36.94) * mm, "end": v(-111.68, 36.54) * mm});
            skLineSegment(sketch, "E1003", {"start": v(-111.92, 37.27) * mm, "end": v(-113.77, 38.68) * mm});
            skLineSegment(sketch, "E1004", {"start": v(-113.77, 38.68) * mm, "end": v(-115.27, 39.96) * mm});
            skArc(sketch, "E1005", {"start": v(-115.27, 39.96) * mm, "mid": v(-115, 40.72) * mm, "end": v(-114.73, 41.49) * mm});
            skLineSegment(sketch, "E1006", {"start": v(-110.43, 41.47) * mm, "end": v(-112.76, 41.54) * mm});
            skLineSegment(sketch, "E1007", {"start": v(-112.76, 41.54) * mm, "end": v(-114.73, 41.49) * mm});
            skArc(sketch, "E1008", {"start": v(-109.78, 41.89) * mm, "mid": v(-110.04, 41.57) * mm, "end": v(-110.43, 41.47) * mm});
            skArc(sketch, "E1009", {"start": v(-109.78, 41.89) * mm, "mid": v(-109.7, 42.1) * mm, "end": v(-109.61, 42.33) * mm});
            skArc(sketch, "E1010", {"start": v(-109.81, 43.08) * mm, "mid": v(-109.59, 42.74) * mm, "end": v(-109.61, 42.33) * mm});
            skLineSegment(sketch, "E1011", {"start": v(-109.81, 43.08) * mm, "end": v(-111.59, 44.58) * mm});
            skLineSegment(sketch, "E1012", {"start": v(-111.59, 44.58) * mm, "end": v(-113.02, 45.94) * mm});
            skArc(sketch, "E1013", {"start": v(-113.02, 45.94) * mm, "mid": v(-112.71, 46.69) * mm, "end": v(-112.4, 47.43) * mm});
            skLineSegment(sketch, "E1014", {"start": v(-108.11, 47.19) * mm, "end": v(-110.43, 47.38) * mm});
            skLineSegment(sketch, "E1015", {"start": v(-110.43, 47.38) * mm, "end": v(-112.4, 47.43) * mm});
            skArc(sketch, "E1016", {"start": v(-107.44, 47.57) * mm, "mid": v(-107.71, 47.27) * mm, "end": v(-108.11, 47.19) * mm});
            skArc(sketch, "E1017", {"start": v(-107.44, 47.57) * mm, "mid": v(-107.34, 47.8) * mm, "end": v(-107.24, 48) * mm});
            skArc(sketch, "E1018", {"start": v(-107.4, 48.77) * mm, "mid": v(-107.2, 48.42) * mm, "end": v(-107.24, 48) * mm});
            skLineSegment(sketch, "E1019", {"start": v(-107.4, 48.77) * mm, "end": v(-109.1, 50.36) * mm});
            skLineSegment(sketch, "E1020", {"start": v(-109.1, 50.36) * mm, "end": v(-110.46, 51.8) * mm});
            skArc(sketch, "E1021", {"start": v(-110.46, 51.8) * mm, "mid": v(-110.12, 52.52) * mm, "end": v(-109.76, 53.25) * mm});
            skLineSegment(sketch, "E1022", {"start": v(-105.5, 52.78) * mm, "end": v(-107.8, 53.1) * mm});
            skLineSegment(sketch, "E1023", {"start": v(-107.8, 53.1) * mm, "end": v(-109.76, 53.25) * mm});
            skArc(sketch, "E1024", {"start": v(-104.8, 53.13) * mm, "mid": v(-105.1, 52.84) * mm, "end": v(-105.5, 52.78) * mm});
            skArc(sketch, "E1025", {"start": v(-104.8, 53.13) * mm, "mid": v(-104.7, 53.34) * mm, "end": v(-104.58, 53.56) * mm});
            skArc(sketch, "E1026", {"start": v(-104.7, 54.32) * mm, "mid": v(-104.52, 53.96) * mm, "end": v(-104.58, 53.56) * mm});
            skLineSegment(sketch, "E1027", {"start": v(-104.7, 54.32) * mm, "end": v(-106.32, 56) * mm});
            skLineSegment(sketch, "E1028", {"start": v(-106.32, 56) * mm, "end": v(-107.6, 57.5) * mm});
            skArc(sketch, "E1029", {"start": v(-107.6, 57.5) * mm, "mid": v(-107.22, 58.21) * mm, "end": v(-106.83, 58.92) * mm});
            skLineSegment(sketch, "E1030", {"start": v(-102.59, 58.23) * mm, "end": v(-104.87, 58.66) * mm});
            skLineSegment(sketch, "E1031", {"start": v(-104.87, 58.66) * mm, "end": v(-106.83, 58.92) * mm});
            skSolve(sketch);
        }
        {
            var Q0;
            Q0 = qSketchRegion(id + "F0", true);
            extrude(context, id + "F1", {"entities" : qUnion([Q0]), "depth" : 5 * mm, "offsetDistance" : 25 * mm});
        }
    });
